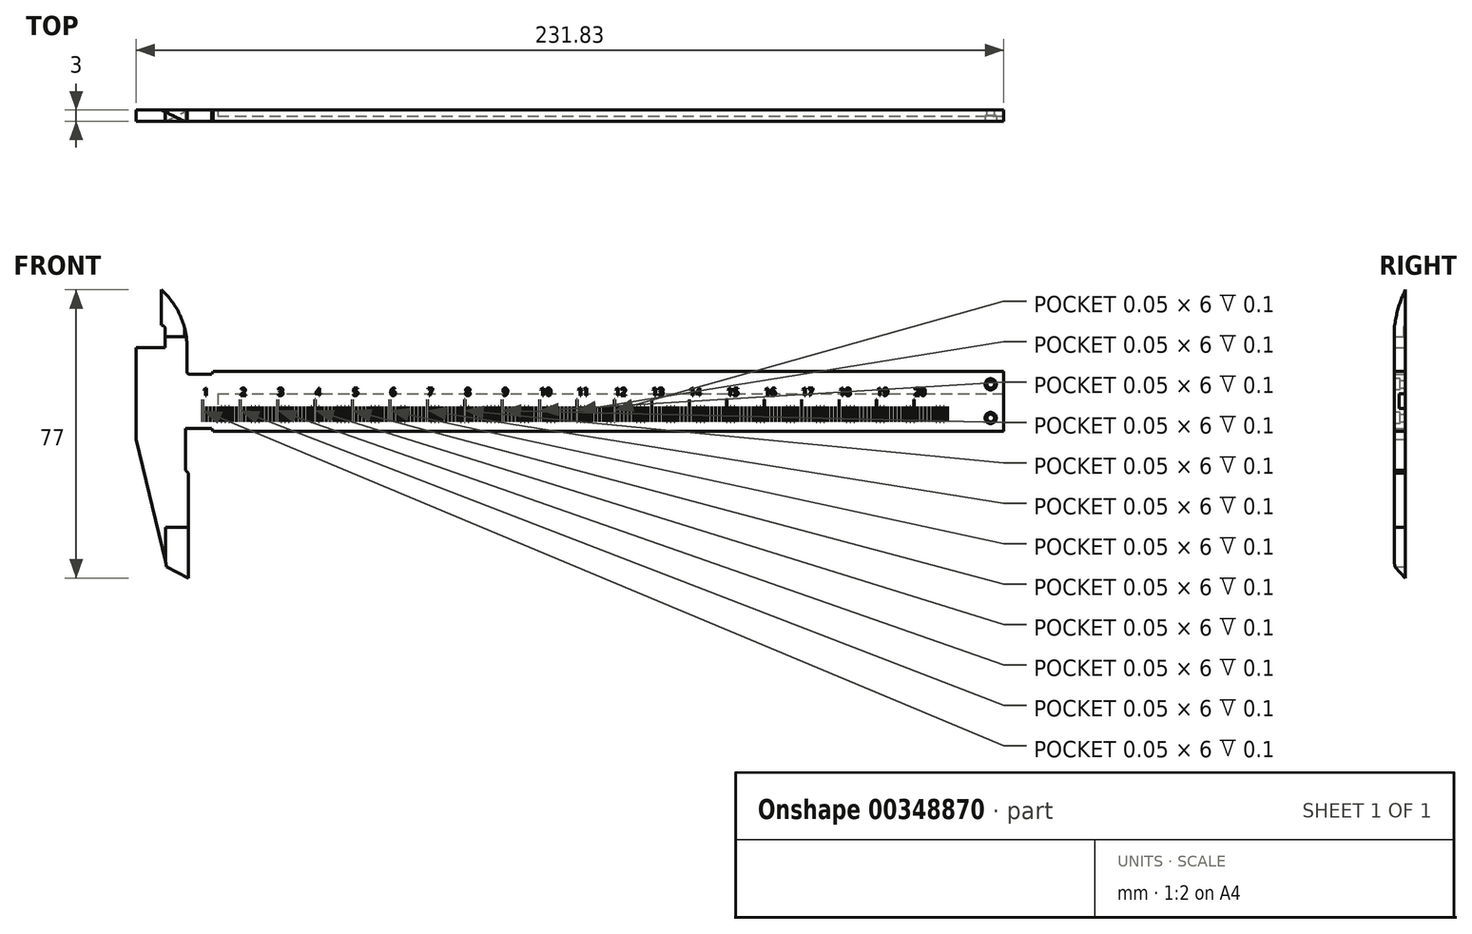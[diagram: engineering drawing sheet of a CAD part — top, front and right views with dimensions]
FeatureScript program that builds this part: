
annotation { "Feature Type Name" : "Feature", "Feature Type Description" : "" }
export const myFeature = defineFeature(function(context is Context, id is Id, definition is map)
    precondition{}
    {
        {
            var Q0;
            Q0=qCreatedBy(makeId("Front.planeOp"),FACE);
            var sketch = newSketch(context, id + "F0", { "sketchPlane" : qUnion([Q0])});
            skLineSegment(sketch, "E0", {"start": v(0, 0) * mm, "end": v(0, 0) * mm});
            skLineSegment(sketch, "E1", {"start": v(0, 8) * mm, "end": v(0, -8) * mm});
            skLineSegment(sketch, "E2", {"start": v(0, -8) * mm, "end": v(-211.2, -8) * mm});
            skLineSegment(sketch, "E3", {"start": v(-211.2, -8) * mm, "end": v(-211.63, -7.25) * mm});
            skLineSegment(sketch, "E4", {"start": v(-211.63, -7.25) * mm, "end": v(-218.63, -7.25) * mm});
            skLineSegment(sketch, "E5.MirrorCS", {"start": v(0, 8) * mm, "end": v(-211.2, 8) * mm});
            skLineSegment(sketch, "E6.MirrorCS", {"start": v(-211.63, 7.25) * mm, "end": v(-217.7, 7.25) * mm});
            skLineSegment(sketch, "E7.MirrorCS", {"start": v(-211.2, 8) * mm, "end": v(-211.63, 7.25) * mm});
            skLineSegment(sketch, "E8", {"start": v(-218.63, -7.25) * mm, "end": v(-218.63, -18.45) * mm});
            skLineSegment(sketch, "E9", {"start": v(-218.63, -18.45) * mm, "end": v(-217.83, -19.25) * mm});
            skLineSegment(sketch, "E10", {"start": v(-217.83, -19.25) * mm, "end": v(-217.83, -47.25) * mm});
            skLineSegment(sketch, "E11", {"start": v(-217.83, -47.25) * mm, "end": v(-223.63, -44.3) * mm});
            skLineSegment(sketch, "E12", {"start": v(-223.63, -44.3) * mm, "end": v(-231.83, -10.25) * mm});
            skLineSegment(sketch, "E13", {"start": v(0, 0) * mm, "end": v(-112.14, 0) * mm});
            skLineSegment(sketch, "E14", {"start": v(-231.83, -10.25) * mm, "end": v(-231.83, 14.25) * mm});
            skLineSegment(sketch, "E15", {"start": v(-231.83, 14.25) * mm, "end": v(-224.03, 14.25) * mm});
            skLineSegment(sketch, "E16", {"start": v(-224.03, 14.25) * mm, "end": v(-224.03, 19.25) * mm});
            skLineSegment(sketch, "E17", {"start": v(-225.03, 20.25) * mm, "end": v(-225.03, 20.25) * mm});
            skLineSegment(sketch, "E18", {"start": v(-225.03, 20.25) * mm, "end": v(-225.03, 29.75) * mm});
            skArc(sketch, "E19", {"start": v(-218.2, 14.25) * mm, "mid": v(-219.99, 22.72) * mm, "end": v(-225.03, 29.75) * mm});
            skLineSegment(sketch, "E20", {"start": v(-218.2, 7.75) * mm, "end": v(-218.2, 14.25) * mm});
            skPoint(sketch, "E21.visualSharp", {"position": v(-224.03, 20.25) * mm});
            skArc(sketch, "E21.filletArc", {"start": v(-224.03, 19.25) * mm, "mid": v(-224.33, 19.96) * mm, "end": v(-225.03, 20.25) * mm});
            skPoint(sketch, "E22.visualSharp", {"position": v(-218.2, 7.25) * mm});
            skArc(sketch, "E22.filletArc", {"start": v(-218.2, 7.75) * mm, "mid": v(-218.06, 7.4) * mm, "end": v(-217.7, 7.25) * mm});
            skSolve(sketch);
        }
        {
            var Q0;
            Q0=qSketchRegion(id+"F0",true);
            extrude(context, id + "F1", {"entities" : qUnion([Q0]), "depth" : 3 * mm});
        }
        {
            var Q0;
            Q0=makeQuery(id+"F1.opExtrude","CAP_FACE",FACE,{"disambiguationData":[OSD([sQuery(id+"F0.wireOp",EDGE,"E1"),sQuery(id+"F0.wireOp",EDGE,"E2"),sQuery(id+"F0.wireOp",EDGE,"E3"),sQuery(id+"F0.wireOp",EDGE,"E4"),sQuery(id+"F0.wireOp",EDGE,"E5.MirrorCS"),sQuery(id+"F0.wireOp",EDGE,"E6.MirrorCS"),sQuery(id+"F0.wireOp",EDGE,"E7.MirrorCS"),sQuery(id+"F0.wireOp",EDGE,"E8"),sQuery(id+"F0.wireOp",EDGE,"E9"),sQuery(id+"F0.wireOp",EDGE,"E10"),sQuery(id+"F0.wireOp",EDGE,"E11"),sQuery(id+"F0.wireOp",EDGE,"E12"),sQuery(id+"F0.wireOp",EDGE,"E14"),sQuery(id+"F0.wireOp",EDGE,"E15"),sQuery(id+"F0.wireOp",EDGE,"E16"),sQuery(id+"F0.wireOp",EDGE,"E17"),sQuery(id+"F0.wireOp",EDGE,"E18"),sQuery(id+"F0.wireOp",EDGE,"E19"),sQuery(id+"F0.wireOp",EDGE,"E20"),sQuery(id+"F0.wireOp",EDGE,"E21.filletArc"),sQuery(id+"F0.wireOp",EDGE,"E22.filletArc")])],"isStart":false});
            var sketch = newSketch(context, id + "F2", { "sketchPlane" : qUnion([Q0])});
            skCircle(sketch, "E23", {"center": v(-3.5, 4.5) * mm, "radius": 1.5 * mm});
            skCircle(sketch, "E24", {"center": v(-3.5, -4.5) * mm, "radius": 1.5 * mm});
            skSolve(sketch);
        }
        {
            var Q0;
            Q0=qSketchRegion(id+"F2",true);
            extrude(context, id + "F3", {"entities" : qUnion([Q0]), "operationType" : NewBodyOperationType.REMOVE, "oppositeDirection" : true, "depth" : 1.5 * mm});
        }
        {
            var Q0;
            Q0=qCreatedBy(makeId("Front.planeOp"),FACE);
            var sketch = newSketch(context, id + "F4", { "sketchPlane" : qUnion([Q0])});
            skCircle(sketch, "E25", {"center": v(-3.5, 4.5) * mm, "radius": 1 * mm});
            skCircle(sketch, "E26", {"center": v(-3.5, -4.5) * mm, "radius": 1 * mm});
            skSolve(sketch);
        }
        {
            var Q0;
            Q0=qSketchRegion(id+"F4",true);
            extrude(context, id + "F5", {"entities" : qUnion([Q0]), "operationType" : NewBodyOperationType.REMOVE, "endBound" : BoundingType.THROUGH_ALL, "depth" : 25 * mm});
        }
        {
            var Q0;
            Q0=makeQuery(id+"F1.opExtrude","SWEPT_FACE",FACE,{"disambiguationData":[OSD([sQuery(id+"F0.wireOp",EDGE,"E15")])]});
            var Q1;
            Q1=makeQuery(id+"F1.opExtrude","CAP_VERTEX",VERTEX,{"disambiguationData":[OSD([sQuery(id+"F0.wireOp",EDGE,"E18"),sQuery(id+"F0.wireOp",EDGE,"E19")])],"isStart":false});
            cPlane(context, id + "F6", {"entities" : qUnion([Q0, Q1]), "cplaneType" : CPlaneType.PLANE_POINT, "offset" : 25 * mm, "width" : 150 * mm, "height" : 150 * mm});
        }
        {
            var Q0;
            Q0=qCreatedBy(id+"F6.planeOp",FACE);
            var sketch = newSketch(context, id + "F7", { "sketchPlane" : qUnion([Q0])});
            skLineSegment(sketch, "E27.0", {"start": v(-225.03, -3) * mm, "end": v(-225.03, 0) * mm});
            skLineSegment(sketch, "E28.0", {"start": v(-218.88, -3) * mm, "end": v(-225.03, -3) * mm});
            skLineSegment(sketch, "E29", {"start": v(-225.03, 0) * mm, "end": v(-218.88, -3) * mm});
            skPoint(sketch, "E30.orphan", {"position": v(-218.2, -3) * mm});
            skSolve(sketch);
        }
        {
            var Q0;
            Q0=qSketchRegion(id+"F7",true);
            extrude(context, id + "F8", {"entities" : qUnion([Q0]), "operationType" : NewBodyOperationType.REMOVE, "oppositeDirection" : true, "depth" : 12.5 * mm});
        }
        {
            var Q0;
            Q0=makeQuery(id+"F1.opExtrude","SWEPT_FACE",FACE,{"disambiguationData":[OSD([sQuery(id+"F0.wireOp",EDGE,"E1")])]});
            var sketch = newSketch(context, id + "F9", { "sketchPlane" : qUnion([Q0])});
            skLineSegment(sketch, "E31", {"start": v(0, 0) * mm, "end": v(-6, 0) * mm, "construction": true});
            skLineSegment(sketch, "E32.bottom", {"start": v(0, -2) * mm, "end": v(-1.65, -2) * mm});
            skLineSegment(sketch, "E32.top", {"start": v(0, 2) * mm, "end": v(-1.65, 2) * mm});
            skLineSegment(sketch, "E32.left", {"start": v(0, -2) * mm, "end": v(0, 2) * mm});
            skLineSegment(sketch, "E32.right", {"start": v(-1.65, -2) * mm, "end": v(-1.65, 2) * mm});
            skSolve(sketch);
        }
        {
            var Q0;
            Q0=qSketchRegion(id+"F9",true);
            extrude(context, id + "F10", {"entities" : qUnion([Q0]), "operationType" : NewBodyOperationType.REMOVE, "oppositeDirection" : true, "depth" : 210 * mm});
        }
        {
            var Q0;
            Q0=makeQuery(id+"F1.opExtrude","SWEPT_FACE",FACE,{"disambiguationData":[OSD([sQuery(id+"F0.wireOp",EDGE,"E2")])]});
            var Q1;
            Q1=makeQuery(id+"F1.opExtrude","CAP_VERTEX",VERTEX,{"disambiguationData":[OSD([sQuery(id+"F0.wireOp",EDGE,"E10"),sQuery(id+"F0.wireOp",EDGE,"E11")])],"isStart":false});
            cPlane(context, id + "F11", {"entities" : qUnion([Q0, Q1]), "cplaneType" : CPlaneType.PLANE_POINT, "offset" : 25 * mm, "width" : 150 * mm, "height" : 150 * mm});
        }
        {
            var Q0;
            Q0=qCreatedBy(id+"F11.planeOp",FACE);
            var sketch = newSketch(context, id + "F12", { "sketchPlane" : qUnion([Q0])});
            skLineSegment(sketch, "E33.0", {"start": v(-217.83, 3) * mm, "end": v(-217.83, 0) * mm});
            skLineSegment(sketch, "E34", {"start": v(-217.83, 3) * mm, "end": v(-223.98, 3) * mm});
            skLineSegment(sketch, "E35", {"start": v(-223.98, 3) * mm, "end": v(-217.83, 0) * mm});
            skSolve(sketch);
        }
        {
            var Q0;
            Q0=qSketchRegion(id+"F12",true);
            extrude(context, id + "F13", {"entities" : qUnion([Q0]), "operationType" : NewBodyOperationType.REMOVE, "oppositeDirection" : true, "depth" : 13.5 * mm});
        }
        {
            var Q0;
            Q0=makeQuery(id+"F1.opExtrude","CAP_FACE",FACE,{"disambiguationData":[OSD([sQuery(id+"F0.wireOp",EDGE,"E1"),sQuery(id+"F0.wireOp",EDGE,"E2"),sQuery(id+"F0.wireOp",EDGE,"E3"),sQuery(id+"F0.wireOp",EDGE,"E4"),sQuery(id+"F0.wireOp",EDGE,"E5.MirrorCS"),sQuery(id+"F0.wireOp",EDGE,"E6.MirrorCS"),sQuery(id+"F0.wireOp",EDGE,"E7.MirrorCS"),sQuery(id+"F0.wireOp",EDGE,"E8"),sQuery(id+"F0.wireOp",EDGE,"E9"),sQuery(id+"F0.wireOp",EDGE,"E10"),sQuery(id+"F0.wireOp",EDGE,"E11"),sQuery(id+"F0.wireOp",EDGE,"E12"),sQuery(id+"F0.wireOp",EDGE,"E14"),sQuery(id+"F0.wireOp",EDGE,"E15"),sQuery(id+"F0.wireOp",EDGE,"E16"),sQuery(id+"F0.wireOp",EDGE,"E17"),sQuery(id+"F0.wireOp",EDGE,"E18"),sQuery(id+"F0.wireOp",EDGE,"E19"),sQuery(id+"F0.wireOp",EDGE,"E20"),sQuery(id+"F0.wireOp",EDGE,"E21.filletArc"),sQuery(id+"F0.wireOp",EDGE,"E22.filletArc")])],"isStart":false});
            var sketch = newSketch(context, id + "F14", { "sketchPlane" : qUnion([Q0])});
            skLineSegment(sketch, "E36.bottom", {"start": v(-214.03, 0.5) * mm, "end": v(-213.98, 0.5) * mm});
            skLineSegment(sketch, "E36.top", {"start": v(-214.03, -5.5) * mm, "end": v(-213.98, -5.5) * mm});
            skLineSegment(sketch, "E36.left", {"start": v(-213.98, 0.5) * mm, "end": v(-213.98, -5.5) * mm});
            skLineSegment(sketch, "E36.right", {"start": v(-214.03, 0.5) * mm, "end": v(-214.03, -5.5) * mm});
            skLineSegment(sketch, "E37.1.0.0", {"start": v(-203.98, 0.5) * mm, "end": v(-203.98, -5.5) * mm});
            skLineSegment(sketch, "E37.1.0.1", {"start": v(-204.03, 0.5) * mm, "end": v(-204.03, -5.5) * mm});
            skLineSegment(sketch, "E37.1.0.2", {"start": v(-204.03, -5.5) * mm, "end": v(-203.98, -5.5) * mm});
            skLineSegment(sketch, "E37.1.0.3", {"start": v(-204.03, 0.5) * mm, "end": v(-203.98, 0.5) * mm});
            skLineSegment(sketch, "E37.2.0.0", {"start": v(-193.98, 0.5) * mm, "end": v(-193.98, -5.5) * mm});
            skLineSegment(sketch, "E37.2.0.1", {"start": v(-194.03, 0.5) * mm, "end": v(-194.03, -5.5) * mm});
            skLineSegment(sketch, "E37.2.0.2", {"start": v(-194.03, -5.5) * mm, "end": v(-193.98, -5.5) * mm});
            skLineSegment(sketch, "E37.2.0.3", {"start": v(-194.03, 0.5) * mm, "end": v(-193.98, 0.5) * mm});
            skLineSegment(sketch, "E37.3.0.0", {"start": v(-183.98, 0.5) * mm, "end": v(-183.98, -5.5) * mm});
            skLineSegment(sketch, "E37.3.0.1", {"start": v(-184.03, 0.5) * mm, "end": v(-184.03, -5.5) * mm});
            skLineSegment(sketch, "E37.3.0.2", {"start": v(-184.03, -5.5) * mm, "end": v(-183.98, -5.5) * mm});
            skLineSegment(sketch, "E37.3.0.3", {"start": v(-184.03, 0.5) * mm, "end": v(-183.98, 0.5) * mm});
            skLineSegment(sketch, "E37.4.0.0", {"start": v(-173.98, 0.5) * mm, "end": v(-173.98, -5.5) * mm});
            skLineSegment(sketch, "E37.4.0.1", {"start": v(-174.03, 0.5) * mm, "end": v(-174.03, -5.5) * mm});
            skLineSegment(sketch, "E37.4.0.2", {"start": v(-174.03, -5.5) * mm, "end": v(-173.98, -5.5) * mm});
            skLineSegment(sketch, "E37.4.0.3", {"start": v(-174.03, 0.5) * mm, "end": v(-173.98, 0.5) * mm});
            skLineSegment(sketch, "E37.5.0.0", {"start": v(-163.98, 0.5) * mm, "end": v(-163.98, -5.5) * mm});
            skLineSegment(sketch, "E37.5.0.1", {"start": v(-164.03, 0.5) * mm, "end": v(-164.03, -5.5) * mm});
            skLineSegment(sketch, "E37.5.0.2", {"start": v(-164.03, -5.5) * mm, "end": v(-163.98, -5.5) * mm});
            skLineSegment(sketch, "E37.5.0.3", {"start": v(-164.03, 0.5) * mm, "end": v(-163.98, 0.5) * mm});
            skLineSegment(sketch, "E37.6.0.0", {"start": v(-153.98, 0.5) * mm, "end": v(-153.98, -5.5) * mm});
            skLineSegment(sketch, "E37.6.0.1", {"start": v(-154.03, 0.5) * mm, "end": v(-154.03, -5.5) * mm});
            skLineSegment(sketch, "E37.6.0.2", {"start": v(-154.03, -5.5) * mm, "end": v(-153.98, -5.5) * mm});
            skLineSegment(sketch, "E37.6.0.3", {"start": v(-154.03, 0.5) * mm, "end": v(-153.98, 0.5) * mm});
            skLineSegment(sketch, "E37.7.0.0", {"start": v(-143.98, 0.5) * mm, "end": v(-143.98, -5.5) * mm});
            skLineSegment(sketch, "E37.7.0.1", {"start": v(-144.03, 0.5) * mm, "end": v(-144.03, -5.5) * mm});
            skLineSegment(sketch, "E37.7.0.2", {"start": v(-144.03, -5.5) * mm, "end": v(-143.98, -5.5) * mm});
            skLineSegment(sketch, "E37.7.0.3", {"start": v(-144.03, 0.5) * mm, "end": v(-143.98, 0.5) * mm});
            skLineSegment(sketch, "E37.8.0.0", {"start": v(-133.98, 0.5) * mm, "end": v(-133.98, -5.5) * mm});
            skLineSegment(sketch, "E37.8.0.1", {"start": v(-134.03, 0.5) * mm, "end": v(-134.03, -5.5) * mm});
            skLineSegment(sketch, "E37.8.0.2", {"start": v(-134.03, -5.5) * mm, "end": v(-133.98, -5.5) * mm});
            skLineSegment(sketch, "E37.8.0.3", {"start": v(-134.03, 0.5) * mm, "end": v(-133.98, 0.5) * mm});
            skLineSegment(sketch, "E37.9.0.0", {"start": v(-123.98, 0.5) * mm, "end": v(-123.98, -5.5) * mm});
            skLineSegment(sketch, "E37.9.0.1", {"start": v(-124.03, 0.5) * mm, "end": v(-124.03, -5.5) * mm});
            skLineSegment(sketch, "E37.9.0.2", {"start": v(-124.03, -5.5) * mm, "end": v(-123.98, -5.5) * mm});
            skLineSegment(sketch, "E37.9.0.3", {"start": v(-124.03, 0.5) * mm, "end": v(-123.98, 0.5) * mm});
            skLineSegment(sketch, "E37.10.0.0", {"start": v(-113.98, 0.5) * mm, "end": v(-113.98, -5.5) * mm});
            skLineSegment(sketch, "E37.10.0.1", {"start": v(-114.03, 0.5) * mm, "end": v(-114.03, -5.5) * mm});
            skLineSegment(sketch, "E37.10.0.2", {"start": v(-114.03, -5.5) * mm, "end": v(-113.98, -5.5) * mm});
            skLineSegment(sketch, "E37.10.0.3", {"start": v(-114.03, 0.5) * mm, "end": v(-113.98, 0.5) * mm});
            skLineSegment(sketch, "E37.11.0.0", {"start": v(-103.98, 0.5) * mm, "end": v(-103.98, -5.5) * mm});
            skLineSegment(sketch, "E37.11.0.1", {"start": v(-104.03, 0.5) * mm, "end": v(-104.03, -5.5) * mm});
            skLineSegment(sketch, "E37.11.0.2", {"start": v(-104.03, -5.5) * mm, "end": v(-103.98, -5.5) * mm});
            skLineSegment(sketch, "E37.11.0.3", {"start": v(-104.03, 0.5) * mm, "end": v(-103.98, 0.5) * mm});
            skLineSegment(sketch, "E37.12.0.0", {"start": v(-93.98, 0.5) * mm, "end": v(-93.98, -5.5) * mm});
            skLineSegment(sketch, "E37.12.0.1", {"start": v(-94.03, 0.5) * mm, "end": v(-94.03, -5.5) * mm});
            skLineSegment(sketch, "E37.12.0.2", {"start": v(-94.03, -5.5) * mm, "end": v(-93.98, -5.5) * mm});
            skLineSegment(sketch, "E37.12.0.3", {"start": v(-94.03, 0.5) * mm, "end": v(-93.98, 0.5) * mm});
            skLineSegment(sketch, "E37.13.0.0", {"start": v(-83.98, 0.5) * mm, "end": v(-83.98, -5.5) * mm});
            skLineSegment(sketch, "E37.13.0.1", {"start": v(-84.03, 0.5) * mm, "end": v(-84.03, -5.5) * mm});
            skLineSegment(sketch, "E37.13.0.2", {"start": v(-84.03, -5.5) * mm, "end": v(-83.98, -5.5) * mm});
            skLineSegment(sketch, "E37.13.0.3", {"start": v(-84.03, 0.5) * mm, "end": v(-83.98, 0.5) * mm});
            skLineSegment(sketch, "E37.14.0.0", {"start": v(-73.98, 0.5) * mm, "end": v(-73.98, -5.5) * mm});
            skLineSegment(sketch, "E37.14.0.1", {"start": v(-74.03, 0.5) * mm, "end": v(-74.03, -5.5) * mm});
            skLineSegment(sketch, "E37.14.0.2", {"start": v(-74.03, -5.5) * mm, "end": v(-73.98, -5.5) * mm});
            skLineSegment(sketch, "E37.14.0.3", {"start": v(-74.03, 0.5) * mm, "end": v(-73.98, 0.5) * mm});
            skLineSegment(sketch, "E37.15.0.0", {"start": v(-63.98, 0.5) * mm, "end": v(-63.98, -5.5) * mm});
            skLineSegment(sketch, "E37.15.0.1", {"start": v(-64.03, 0.5) * mm, "end": v(-64.03, -5.5) * mm});
            skLineSegment(sketch, "E37.15.0.2", {"start": v(-64.03, -5.5) * mm, "end": v(-63.98, -5.5) * mm});
            skLineSegment(sketch, "E37.15.0.3", {"start": v(-64.03, 0.5) * mm, "end": v(-63.98, 0.5) * mm});
            skLineSegment(sketch, "E37.16.0.0", {"start": v(-53.98, 0.5) * mm, "end": v(-53.98, -5.5) * mm});
            skLineSegment(sketch, "E37.16.0.1", {"start": v(-54.03, 0.5) * mm, "end": v(-54.03, -5.5) * mm});
            skLineSegment(sketch, "E37.16.0.2", {"start": v(-54.03, -5.5) * mm, "end": v(-53.98, -5.5) * mm});
            skLineSegment(sketch, "E37.16.0.3", {"start": v(-54.03, 0.5) * mm, "end": v(-53.98, 0.5) * mm});
            skLineSegment(sketch, "E37.17.0.0", {"start": v(-43.98, 0.5) * mm, "end": v(-43.98, -5.5) * mm});
            skLineSegment(sketch, "E37.17.0.1", {"start": v(-44.03, 0.5) * mm, "end": v(-44.03, -5.5) * mm});
            skLineSegment(sketch, "E37.17.0.2", {"start": v(-44.03, -5.5) * mm, "end": v(-43.98, -5.5) * mm});
            skLineSegment(sketch, "E37.17.0.3", {"start": v(-44.03, 0.5) * mm, "end": v(-43.98, 0.5) * mm});
            skLineSegment(sketch, "E37.18.0.0", {"start": v(-33.98, 0.5) * mm, "end": v(-33.98, -5.5) * mm});
            skLineSegment(sketch, "E37.18.0.1", {"start": v(-34.03, 0.5) * mm, "end": v(-34.03, -5.5) * mm});
            skLineSegment(sketch, "E37.18.0.2", {"start": v(-34.03, -5.5) * mm, "end": v(-33.98, -5.5) * mm});
            skLineSegment(sketch, "E37.18.0.3", {"start": v(-34.03, 0.5) * mm, "end": v(-33.98, 0.5) * mm});
            skLineSegment(sketch, "E37.19.0.0", {"start": v(-23.98, 0.5) * mm, "end": v(-23.98, -5.5) * mm});
            skLineSegment(sketch, "E37.19.0.1", {"start": v(-24.03, 0.5) * mm, "end": v(-24.03, -5.5) * mm});
            skLineSegment(sketch, "E37.19.0.2", {"start": v(-24.03, -5.5) * mm, "end": v(-23.98, -5.5) * mm});
            skLineSegment(sketch, "E37.19.0.3", {"start": v(-24.03, 0.5) * mm, "end": v(-23.98, 0.5) * mm});
            skLineSegment(sketch, "E37.direction1", {"start": v(-214.03, -5.5) * mm, "end": v(-204.03, -5.5) * mm, "construction": true});
            skLineSegment(sketch, "E38.bottom", {"start": v(-213.03, -1.5) * mm, "end": v(-212.98, -1.5) * mm});
            skLineSegment(sketch, "E38.top", {"start": v(-213.03, -5.5) * mm, "end": v(-212.98, -5.5) * mm});
            skLineSegment(sketch, "E38.left", {"start": v(-213.03, -1.5) * mm, "end": v(-213.03, -5.5) * mm});
            skLineSegment(sketch, "E38.right", {"start": v(-212.98, -1.5) * mm, "end": v(-212.98, -5.5) * mm});
            skLineSegment(sketch, "E39.1.0.0", {"start": v(-211.98, -1.5) * mm, "end": v(-211.98, -5.5) * mm});
            skLineSegment(sketch, "E39.1.0.1", {"start": v(-212.03, -1.5) * mm, "end": v(-212.03, -5.5) * mm});
            skLineSegment(sketch, "E39.1.0.2", {"start": v(-212.03, -1.5) * mm, "end": v(-211.98, -1.5) * mm});
            skLineSegment(sketch, "E39.1.0.3", {"start": v(-212.03, -5.5) * mm, "end": v(-211.98, -5.5) * mm});
            skLineSegment(sketch, "E39.2.0.0", {"start": v(-210.98, -1.5) * mm, "end": v(-210.98, -5.5) * mm});
            skLineSegment(sketch, "E39.2.0.1", {"start": v(-211.03, -1.5) * mm, "end": v(-211.03, -5.5) * mm});
            skLineSegment(sketch, "E39.2.0.2", {"start": v(-211.03, -1.5) * mm, "end": v(-210.98, -1.5) * mm});
            skLineSegment(sketch, "E39.2.0.3", {"start": v(-211.03, -5.5) * mm, "end": v(-210.98, -5.5) * mm});
            skLineSegment(sketch, "E39.3.0.0", {"start": v(-209.98, -1.5) * mm, "end": v(-209.98, -5.5) * mm});
            skLineSegment(sketch, "E39.3.0.1", {"start": v(-210.03, -1.5) * mm, "end": v(-210.03, -5.5) * mm});
            skLineSegment(sketch, "E39.3.0.2", {"start": v(-210.03, -1.5) * mm, "end": v(-209.98, -1.5) * mm});
            skLineSegment(sketch, "E39.3.0.3", {"start": v(-210.03, -5.5) * mm, "end": v(-209.98, -5.5) * mm});
            skLineSegment(sketch, "E39.4.0.0", {"start": v(-208.98, -1.5) * mm, "end": v(-208.98, -5.5) * mm});
            skLineSegment(sketch, "E39.4.0.1", {"start": v(-209.03, -1.5) * mm, "end": v(-209.03, -5.5) * mm});
            skLineSegment(sketch, "E39.4.0.2", {"start": v(-209.03, -1.5) * mm, "end": v(-208.98, -1.5) * mm});
            skLineSegment(sketch, "E39.4.0.3", {"start": v(-209.03, -5.5) * mm, "end": v(-208.98, -5.5) * mm});
            skLineSegment(sketch, "E39.5.0.0", {"start": v(-207.98, -1.5) * mm, "end": v(-207.98, -5.5) * mm});
            skLineSegment(sketch, "E39.5.0.1", {"start": v(-208.03, -1.5) * mm, "end": v(-208.03, -5.5) * mm});
            skLineSegment(sketch, "E39.5.0.2", {"start": v(-208.03, -1.5) * mm, "end": v(-207.98, -1.5) * mm});
            skLineSegment(sketch, "E39.5.0.3", {"start": v(-208.03, -5.5) * mm, "end": v(-207.98, -5.5) * mm});
            skLineSegment(sketch, "E39.6.0.0", {"start": v(-206.98, -1.5) * mm, "end": v(-206.98, -5.5) * mm});
            skLineSegment(sketch, "E39.6.0.1", {"start": v(-207.03, -1.5) * mm, "end": v(-207.03, -5.5) * mm});
            skLineSegment(sketch, "E39.6.0.2", {"start": v(-207.03, -1.5) * mm, "end": v(-206.98, -1.5) * mm});
            skLineSegment(sketch, "E39.6.0.3", {"start": v(-207.03, -5.5) * mm, "end": v(-206.98, -5.5) * mm});
            skLineSegment(sketch, "E39.7.0.0", {"start": v(-205.98, -1.5) * mm, "end": v(-205.98, -5.5) * mm});
            skLineSegment(sketch, "E39.7.0.1", {"start": v(-206.03, -1.5) * mm, "end": v(-206.03, -5.5) * mm});
            skLineSegment(sketch, "E39.7.0.2", {"start": v(-206.03, -1.5) * mm, "end": v(-205.98, -1.5) * mm});
            skLineSegment(sketch, "E39.7.0.3", {"start": v(-206.03, -5.5) * mm, "end": v(-205.98, -5.5) * mm});
            skLineSegment(sketch, "E39.8.0.0", {"start": v(-204.98, -1.5) * mm, "end": v(-204.98, -5.5) * mm});
            skLineSegment(sketch, "E39.8.0.1", {"start": v(-205.03, -1.5) * mm, "end": v(-205.03, -5.5) * mm});
            skLineSegment(sketch, "E39.8.0.2", {"start": v(-205.03, -1.5) * mm, "end": v(-204.98, -1.5) * mm});
            skLineSegment(sketch, "E39.8.0.3", {"start": v(-205.03, -5.5) * mm, "end": v(-204.98, -5.5) * mm});
            skLineSegment(sketch, "E39.direction1", {"start": v(-213.03, -5.5) * mm, "end": v(-212.03, -5.5) * mm, "construction": true});
            skLineSegment(sketch, "E40.1.0.0", {"start": v(-202.03, -1.5) * mm, "end": v(-202.03, -5.5) * mm});
            skLineSegment(sketch, "E40.1.0.1", {"start": v(-198.03, -1.5) * mm, "end": v(-198.03, -5.5) * mm});
            skLineSegment(sketch, "E40.1.0.2", {"start": v(-203.03, -5.5) * mm, "end": v(-202.03, -5.5) * mm, "construction": true});
            skLineSegment(sketch, "E40.1.0.3", {"start": v(-201.98, -1.5) * mm, "end": v(-201.98, -5.5) * mm});
            skLineSegment(sketch, "E40.1.0.4", {"start": v(-197.98, -1.5) * mm, "end": v(-197.98, -5.5) * mm});
            skLineSegment(sketch, "E40.1.0.5", {"start": v(-202.98, -1.5) * mm, "end": v(-202.98, -5.5) * mm});
            skLineSegment(sketch, "E40.1.0.6", {"start": v(-197.03, -1.5) * mm, "end": v(-197.03, -5.5) * mm});
            skLineSegment(sketch, "E40.1.0.7", {"start": v(-201.03, -1.5) * mm, "end": v(-201.03, -5.5) * mm});
            skLineSegment(sketch, "E40.1.0.8", {"start": v(-199.98, -1.5) * mm, "end": v(-199.98, -5.5) * mm});
            skLineSegment(sketch, "E40.1.0.9", {"start": v(-195.98, -1.5) * mm, "end": v(-195.98, -5.5) * mm});
            skLineSegment(sketch, "E40.1.0.10", {"start": v(-200.03, -1.5) * mm, "end": v(-200.03, -5.5) * mm});
            skLineSegment(sketch, "E40.1.0.11", {"start": v(-196.03, -1.5) * mm, "end": v(-196.03, -5.5) * mm});
            skLineSegment(sketch, "E40.1.0.12", {"start": v(-195.03, -1.5) * mm, "end": v(-195.03, -5.5) * mm});
            skLineSegment(sketch, "E40.1.0.13", {"start": v(-199.03, -1.5) * mm, "end": v(-199.03, -5.5) * mm});
            skLineSegment(sketch, "E40.1.0.14", {"start": v(-196.98, -1.5) * mm, "end": v(-196.98, -5.5) * mm});
            skLineSegment(sketch, "E40.1.0.15", {"start": v(-200.98, -1.5) * mm, "end": v(-200.98, -5.5) * mm});
            skLineSegment(sketch, "E40.1.0.16", {"start": v(-198.98, -1.5) * mm, "end": v(-198.98, -5.5) * mm});
            skLineSegment(sketch, "E40.1.0.17", {"start": v(-194.98, -1.5) * mm, "end": v(-194.98, -5.5) * mm});
            skLineSegment(sketch, "E40.1.0.18", {"start": v(-203.03, -1.5) * mm, "end": v(-203.03, -5.5) * mm});
            skLineSegment(sketch, "E40.1.0.19", {"start": v(-198.03, -5.5) * mm, "end": v(-197.98, -5.5) * mm});
            skLineSegment(sketch, "E40.1.0.20", {"start": v(-202.03, -1.5) * mm, "end": v(-201.98, -1.5) * mm});
            skLineSegment(sketch, "E40.1.0.21", {"start": v(-198.03, -1.5) * mm, "end": v(-197.98, -1.5) * mm});
            skLineSegment(sketch, "E40.1.0.22", {"start": v(-200.03, -1.5) * mm, "end": v(-199.98, -1.5) * mm});
            skLineSegment(sketch, "E40.1.0.23", {"start": v(-196.03, -1.5) * mm, "end": v(-195.98, -1.5) * mm});
            skLineSegment(sketch, "E40.1.0.24", {"start": v(-200.03, -5.5) * mm, "end": v(-199.98, -5.5) * mm});
            skLineSegment(sketch, "E40.1.0.25", {"start": v(-196.03, -5.5) * mm, "end": v(-195.98, -5.5) * mm});
            skLineSegment(sketch, "E40.1.0.26", {"start": v(-202.03, -5.5) * mm, "end": v(-201.98, -5.5) * mm});
            skLineSegment(sketch, "E40.1.0.27", {"start": v(-195.03, -5.5) * mm, "end": v(-194.98, -5.5) * mm});
            skLineSegment(sketch, "E40.1.0.28", {"start": v(-199.03, -5.5) * mm, "end": v(-198.98, -5.5) * mm});
            skLineSegment(sketch, "E40.1.0.29", {"start": v(-197.03, -1.5) * mm, "end": v(-196.98, -1.5) * mm});
            skLineSegment(sketch, "E40.1.0.30", {"start": v(-201.03, -1.5) * mm, "end": v(-200.98, -1.5) * mm});
            skLineSegment(sketch, "E40.1.0.31", {"start": v(-197.03, -5.5) * mm, "end": v(-196.98, -5.5) * mm});
            skLineSegment(sketch, "E40.1.0.32", {"start": v(-201.03, -5.5) * mm, "end": v(-200.98, -5.5) * mm});
            skLineSegment(sketch, "E40.1.0.33", {"start": v(-203.03, -1.5) * mm, "end": v(-202.98, -1.5) * mm});
            skLineSegment(sketch, "E40.1.0.34", {"start": v(-199.03, -1.5) * mm, "end": v(-198.98, -1.5) * mm});
            skLineSegment(sketch, "E40.1.0.35", {"start": v(-195.03, -1.5) * mm, "end": v(-194.98, -1.5) * mm});
            skLineSegment(sketch, "E40.1.0.36", {"start": v(-203.03, -5.5) * mm, "end": v(-202.98, -5.5) * mm});
            skLineSegment(sketch, "E40.2.0.0", {"start": v(-192.03, -1.5) * mm, "end": v(-192.03, -5.5) * mm});
            skLineSegment(sketch, "E40.2.0.1", {"start": v(-188.03, -1.5) * mm, "end": v(-188.03, -5.5) * mm});
            skLineSegment(sketch, "E40.2.0.2", {"start": v(-193.03, -5.5) * mm, "end": v(-192.03, -5.5) * mm, "construction": true});
            skLineSegment(sketch, "E40.2.0.3", {"start": v(-191.98, -1.5) * mm, "end": v(-191.98, -5.5) * mm});
            skLineSegment(sketch, "E40.2.0.4", {"start": v(-187.98, -1.5) * mm, "end": v(-187.98, -5.5) * mm});
            skLineSegment(sketch, "E40.2.0.5", {"start": v(-192.98, -1.5) * mm, "end": v(-192.98, -5.5) * mm});
            skLineSegment(sketch, "E40.2.0.6", {"start": v(-187.03, -1.5) * mm, "end": v(-187.03, -5.5) * mm});
            skLineSegment(sketch, "E40.2.0.7", {"start": v(-191.03, -1.5) * mm, "end": v(-191.03, -5.5) * mm});
            skLineSegment(sketch, "E40.2.0.8", {"start": v(-189.98, -1.5) * mm, "end": v(-189.98, -5.5) * mm});
            skLineSegment(sketch, "E40.2.0.9", {"start": v(-185.98, -1.5) * mm, "end": v(-185.98, -5.5) * mm});
            skLineSegment(sketch, "E40.2.0.10", {"start": v(-190.03, -1.5) * mm, "end": v(-190.03, -5.5) * mm});
            skLineSegment(sketch, "E40.2.0.11", {"start": v(-186.03, -1.5) * mm, "end": v(-186.03, -5.5) * mm});
            skLineSegment(sketch, "E40.2.0.12", {"start": v(-185.03, -1.5) * mm, "end": v(-185.03, -5.5) * mm});
            skLineSegment(sketch, "E40.2.0.13", {"start": v(-189.03, -1.5) * mm, "end": v(-189.03, -5.5) * mm});
            skLineSegment(sketch, "E40.2.0.14", {"start": v(-186.98, -1.5) * mm, "end": v(-186.98, -5.5) * mm});
            skLineSegment(sketch, "E40.2.0.15", {"start": v(-190.98, -1.5) * mm, "end": v(-190.98, -5.5) * mm});
            skLineSegment(sketch, "E40.2.0.16", {"start": v(-188.98, -1.5) * mm, "end": v(-188.98, -5.5) * mm});
            skLineSegment(sketch, "E40.2.0.17", {"start": v(-184.98, -1.5) * mm, "end": v(-184.98, -5.5) * mm});
            skLineSegment(sketch, "E40.2.0.18", {"start": v(-193.03, -1.5) * mm, "end": v(-193.03, -5.5) * mm});
            skLineSegment(sketch, "E40.2.0.19", {"start": v(-188.03, -5.5) * mm, "end": v(-187.98, -5.5) * mm});
            skLineSegment(sketch, "E40.2.0.20", {"start": v(-192.03, -1.5) * mm, "end": v(-191.98, -1.5) * mm});
            skLineSegment(sketch, "E40.2.0.21", {"start": v(-188.03, -1.5) * mm, "end": v(-187.98, -1.5) * mm});
            skLineSegment(sketch, "E40.2.0.22", {"start": v(-190.03, -1.5) * mm, "end": v(-189.98, -1.5) * mm});
            skLineSegment(sketch, "E40.2.0.23", {"start": v(-186.03, -1.5) * mm, "end": v(-185.98, -1.5) * mm});
            skLineSegment(sketch, "E40.2.0.24", {"start": v(-190.03, -5.5) * mm, "end": v(-189.98, -5.5) * mm});
            skLineSegment(sketch, "E40.2.0.25", {"start": v(-186.03, -5.5) * mm, "end": v(-185.98, -5.5) * mm});
            skLineSegment(sketch, "E40.2.0.26", {"start": v(-192.03, -5.5) * mm, "end": v(-191.98, -5.5) * mm});
            skLineSegment(sketch, "E40.2.0.27", {"start": v(-185.03, -5.5) * mm, "end": v(-184.98, -5.5) * mm});
            skLineSegment(sketch, "E40.2.0.28", {"start": v(-189.03, -5.5) * mm, "end": v(-188.98, -5.5) * mm});
            skLineSegment(sketch, "E40.2.0.29", {"start": v(-187.03, -1.5) * mm, "end": v(-186.98, -1.5) * mm});
            skLineSegment(sketch, "E40.2.0.30", {"start": v(-191.03, -1.5) * mm, "end": v(-190.98, -1.5) * mm});
            skLineSegment(sketch, "E40.2.0.31", {"start": v(-187.03, -5.5) * mm, "end": v(-186.98, -5.5) * mm});
            skLineSegment(sketch, "E40.2.0.32", {"start": v(-191.03, -5.5) * mm, "end": v(-190.98, -5.5) * mm});
            skLineSegment(sketch, "E40.2.0.33", {"start": v(-193.03, -1.5) * mm, "end": v(-192.98, -1.5) * mm});
            skLineSegment(sketch, "E40.2.0.34", {"start": v(-189.03, -1.5) * mm, "end": v(-188.98, -1.5) * mm});
            skLineSegment(sketch, "E40.2.0.35", {"start": v(-185.03, -1.5) * mm, "end": v(-184.98, -1.5) * mm});
            skLineSegment(sketch, "E40.2.0.36", {"start": v(-193.03, -5.5) * mm, "end": v(-192.98, -5.5) * mm});
            skLineSegment(sketch, "E40.3.0.0", {"start": v(-182.03, -1.5) * mm, "end": v(-182.03, -5.5) * mm});
            skLineSegment(sketch, "E40.3.0.1", {"start": v(-178.03, -1.5) * mm, "end": v(-178.03, -5.5) * mm});
            skLineSegment(sketch, "E40.3.0.2", {"start": v(-183.03, -5.5) * mm, "end": v(-182.03, -5.5) * mm, "construction": true});
            skLineSegment(sketch, "E40.3.0.3", {"start": v(-181.98, -1.5) * mm, "end": v(-181.98, -5.5) * mm});
            skLineSegment(sketch, "E40.3.0.4", {"start": v(-177.98, -1.5) * mm, "end": v(-177.98, -5.5) * mm});
            skLineSegment(sketch, "E40.3.0.5", {"start": v(-182.98, -1.5) * mm, "end": v(-182.98, -5.5) * mm});
            skLineSegment(sketch, "E40.3.0.6", {"start": v(-177.03, -1.5) * mm, "end": v(-177.03, -5.5) * mm});
            skLineSegment(sketch, "E40.3.0.7", {"start": v(-181.03, -1.5) * mm, "end": v(-181.03, -5.5) * mm});
            skLineSegment(sketch, "E40.3.0.8", {"start": v(-179.98, -1.5) * mm, "end": v(-179.98, -5.5) * mm});
            skLineSegment(sketch, "E40.3.0.9", {"start": v(-175.98, -1.5) * mm, "end": v(-175.98, -5.5) * mm});
            skLineSegment(sketch, "E40.3.0.10", {"start": v(-180.03, -1.5) * mm, "end": v(-180.03, -5.5) * mm});
            skLineSegment(sketch, "E40.3.0.11", {"start": v(-176.03, -1.5) * mm, "end": v(-176.03, -5.5) * mm});
            skLineSegment(sketch, "E40.3.0.12", {"start": v(-175.03, -1.5) * mm, "end": v(-175.03, -5.5) * mm});
            skLineSegment(sketch, "E40.3.0.13", {"start": v(-179.03, -1.5) * mm, "end": v(-179.03, -5.5) * mm});
            skLineSegment(sketch, "E40.3.0.14", {"start": v(-176.98, -1.5) * mm, "end": v(-176.98, -5.5) * mm});
            skLineSegment(sketch, "E40.3.0.15", {"start": v(-180.98, -1.5) * mm, "end": v(-180.98, -5.5) * mm});
            skLineSegment(sketch, "E40.3.0.16", {"start": v(-178.98, -1.5) * mm, "end": v(-178.98, -5.5) * mm});
            skLineSegment(sketch, "E40.3.0.17", {"start": v(-174.98, -1.5) * mm, "end": v(-174.98, -5.5) * mm});
            skLineSegment(sketch, "E40.3.0.18", {"start": v(-183.03, -1.5) * mm, "end": v(-183.03, -5.5) * mm});
            skLineSegment(sketch, "E40.3.0.19", {"start": v(-178.03, -5.5) * mm, "end": v(-177.98, -5.5) * mm});
            skLineSegment(sketch, "E40.3.0.20", {"start": v(-182.03, -1.5) * mm, "end": v(-181.98, -1.5) * mm});
            skLineSegment(sketch, "E40.3.0.21", {"start": v(-178.03, -1.5) * mm, "end": v(-177.98, -1.5) * mm});
            skLineSegment(sketch, "E40.3.0.22", {"start": v(-180.03, -1.5) * mm, "end": v(-179.98, -1.5) * mm});
            skLineSegment(sketch, "E40.3.0.23", {"start": v(-176.03, -1.5) * mm, "end": v(-175.98, -1.5) * mm});
            skLineSegment(sketch, "E40.3.0.24", {"start": v(-180.03, -5.5) * mm, "end": v(-179.98, -5.5) * mm});
            skLineSegment(sketch, "E40.3.0.25", {"start": v(-176.03, -5.5) * mm, "end": v(-175.98, -5.5) * mm});
            skLineSegment(sketch, "E40.3.0.26", {"start": v(-182.03, -5.5) * mm, "end": v(-181.98, -5.5) * mm});
            skLineSegment(sketch, "E40.3.0.27", {"start": v(-175.03, -5.5) * mm, "end": v(-174.98, -5.5) * mm});
            skLineSegment(sketch, "E40.3.0.28", {"start": v(-179.03, -5.5) * mm, "end": v(-178.98, -5.5) * mm});
            skLineSegment(sketch, "E40.3.0.29", {"start": v(-177.03, -1.5) * mm, "end": v(-176.98, -1.5) * mm});
            skLineSegment(sketch, "E40.3.0.30", {"start": v(-181.03, -1.5) * mm, "end": v(-180.98, -1.5) * mm});
            skLineSegment(sketch, "E40.3.0.31", {"start": v(-177.03, -5.5) * mm, "end": v(-176.98, -5.5) * mm});
            skLineSegment(sketch, "E40.3.0.32", {"start": v(-181.03, -5.5) * mm, "end": v(-180.98, -5.5) * mm});
            skLineSegment(sketch, "E40.3.0.33", {"start": v(-183.03, -1.5) * mm, "end": v(-182.98, -1.5) * mm});
            skLineSegment(sketch, "E40.3.0.34", {"start": v(-179.03, -1.5) * mm, "end": v(-178.98, -1.5) * mm});
            skLineSegment(sketch, "E40.3.0.35", {"start": v(-175.03, -1.5) * mm, "end": v(-174.98, -1.5) * mm});
            skLineSegment(sketch, "E40.3.0.36", {"start": v(-183.03, -5.5) * mm, "end": v(-182.98, -5.5) * mm});
            skLineSegment(sketch, "E40.4.0.0", {"start": v(-172.03, -1.5) * mm, "end": v(-172.03, -5.5) * mm});
            skLineSegment(sketch, "E40.4.0.1", {"start": v(-168.03, -1.5) * mm, "end": v(-168.03, -5.5) * mm});
            skLineSegment(sketch, "E40.4.0.2", {"start": v(-173.03, -5.5) * mm, "end": v(-172.03, -5.5) * mm, "construction": true});
            skLineSegment(sketch, "E40.4.0.3", {"start": v(-171.98, -1.5) * mm, "end": v(-171.98, -5.5) * mm});
            skLineSegment(sketch, "E40.4.0.4", {"start": v(-167.98, -1.5) * mm, "end": v(-167.98, -5.5) * mm});
            skLineSegment(sketch, "E40.4.0.5", {"start": v(-172.98, -1.5) * mm, "end": v(-172.98, -5.5) * mm});
            skLineSegment(sketch, "E40.4.0.6", {"start": v(-167.03, -1.5) * mm, "end": v(-167.03, -5.5) * mm});
            skLineSegment(sketch, "E40.4.0.7", {"start": v(-171.03, -1.5) * mm, "end": v(-171.03, -5.5) * mm});
            skLineSegment(sketch, "E40.4.0.8", {"start": v(-169.98, -1.5) * mm, "end": v(-169.98, -5.5) * mm});
            skLineSegment(sketch, "E40.4.0.9", {"start": v(-165.98, -1.5) * mm, "end": v(-165.98, -5.5) * mm});
            skLineSegment(sketch, "E40.4.0.10", {"start": v(-170.03, -1.5) * mm, "end": v(-170.03, -5.5) * mm});
            skLineSegment(sketch, "E40.4.0.11", {"start": v(-166.03, -1.5) * mm, "end": v(-166.03, -5.5) * mm});
            skLineSegment(sketch, "E40.4.0.12", {"start": v(-165.03, -1.5) * mm, "end": v(-165.03, -5.5) * mm});
            skLineSegment(sketch, "E40.4.0.13", {"start": v(-169.03, -1.5) * mm, "end": v(-169.03, -5.5) * mm});
            skLineSegment(sketch, "E40.4.0.14", {"start": v(-166.98, -1.5) * mm, "end": v(-166.98, -5.5) * mm});
            skLineSegment(sketch, "E40.4.0.15", {"start": v(-170.98, -1.5) * mm, "end": v(-170.98, -5.5) * mm});
            skLineSegment(sketch, "E40.4.0.16", {"start": v(-168.98, -1.5) * mm, "end": v(-168.98, -5.5) * mm});
            skLineSegment(sketch, "E40.4.0.17", {"start": v(-164.98, -1.5) * mm, "end": v(-164.98, -5.5) * mm});
            skLineSegment(sketch, "E40.4.0.18", {"start": v(-173.03, -1.5) * mm, "end": v(-173.03, -5.5) * mm});
            skLineSegment(sketch, "E40.4.0.19", {"start": v(-168.03, -5.5) * mm, "end": v(-167.98, -5.5) * mm});
            skLineSegment(sketch, "E40.4.0.20", {"start": v(-172.03, -1.5) * mm, "end": v(-171.98, -1.5) * mm});
            skLineSegment(sketch, "E40.4.0.21", {"start": v(-168.03, -1.5) * mm, "end": v(-167.98, -1.5) * mm});
            skLineSegment(sketch, "E40.4.0.22", {"start": v(-170.03, -1.5) * mm, "end": v(-169.98, -1.5) * mm});
            skLineSegment(sketch, "E40.4.0.23", {"start": v(-166.03, -1.5) * mm, "end": v(-165.98, -1.5) * mm});
            skLineSegment(sketch, "E40.4.0.24", {"start": v(-170.03, -5.5) * mm, "end": v(-169.98, -5.5) * mm});
            skLineSegment(sketch, "E40.4.0.25", {"start": v(-166.03, -5.5) * mm, "end": v(-165.98, -5.5) * mm});
            skLineSegment(sketch, "E40.4.0.26", {"start": v(-172.03, -5.5) * mm, "end": v(-171.98, -5.5) * mm});
            skLineSegment(sketch, "E40.4.0.27", {"start": v(-165.03, -5.5) * mm, "end": v(-164.98, -5.5) * mm});
            skLineSegment(sketch, "E40.4.0.28", {"start": v(-169.03, -5.5) * mm, "end": v(-168.98, -5.5) * mm});
            skLineSegment(sketch, "E40.4.0.29", {"start": v(-167.03, -1.5) * mm, "end": v(-166.98, -1.5) * mm});
            skLineSegment(sketch, "E40.4.0.30", {"start": v(-171.03, -1.5) * mm, "end": v(-170.98, -1.5) * mm});
            skLineSegment(sketch, "E40.4.0.31", {"start": v(-167.03, -5.5) * mm, "end": v(-166.98, -5.5) * mm});
            skLineSegment(sketch, "E40.4.0.32", {"start": v(-171.03, -5.5) * mm, "end": v(-170.98, -5.5) * mm});
            skLineSegment(sketch, "E40.4.0.33", {"start": v(-173.03, -1.5) * mm, "end": v(-172.98, -1.5) * mm});
            skLineSegment(sketch, "E40.4.0.34", {"start": v(-169.03, -1.5) * mm, "end": v(-168.98, -1.5) * mm});
            skLineSegment(sketch, "E40.4.0.35", {"start": v(-165.03, -1.5) * mm, "end": v(-164.98, -1.5) * mm});
            skLineSegment(sketch, "E40.4.0.36", {"start": v(-173.03, -5.5) * mm, "end": v(-172.98, -5.5) * mm});
            skLineSegment(sketch, "E40.5.0.0", {"start": v(-162.03, -1.5) * mm, "end": v(-162.03, -5.5) * mm});
            skLineSegment(sketch, "E40.5.0.1", {"start": v(-158.03, -1.5) * mm, "end": v(-158.03, -5.5) * mm});
            skLineSegment(sketch, "E40.5.0.2", {"start": v(-163.03, -5.5) * mm, "end": v(-162.03, -5.5) * mm, "construction": true});
            skLineSegment(sketch, "E40.5.0.3", {"start": v(-161.98, -1.5) * mm, "end": v(-161.98, -5.5) * mm});
            skLineSegment(sketch, "E40.5.0.4", {"start": v(-157.98, -1.5) * mm, "end": v(-157.98, -5.5) * mm});
            skLineSegment(sketch, "E40.5.0.5", {"start": v(-162.98, -1.5) * mm, "end": v(-162.98, -5.5) * mm});
            skLineSegment(sketch, "E40.5.0.6", {"start": v(-157.03, -1.5) * mm, "end": v(-157.03, -5.5) * mm});
            skLineSegment(sketch, "E40.5.0.7", {"start": v(-161.03, -1.5) * mm, "end": v(-161.03, -5.5) * mm});
            skLineSegment(sketch, "E40.5.0.8", {"start": v(-159.98, -1.5) * mm, "end": v(-159.98, -5.5) * mm});
            skLineSegment(sketch, "E40.5.0.9", {"start": v(-155.98, -1.5) * mm, "end": v(-155.98, -5.5) * mm});
            skLineSegment(sketch, "E40.5.0.10", {"start": v(-160.03, -1.5) * mm, "end": v(-160.03, -5.5) * mm});
            skLineSegment(sketch, "E40.5.0.11", {"start": v(-156.03, -1.5) * mm, "end": v(-156.03, -5.5) * mm});
            skLineSegment(sketch, "E40.5.0.12", {"start": v(-155.03, -1.5) * mm, "end": v(-155.03, -5.5) * mm});
            skLineSegment(sketch, "E40.5.0.13", {"start": v(-159.03, -1.5) * mm, "end": v(-159.03, -5.5) * mm});
            skLineSegment(sketch, "E40.5.0.14", {"start": v(-156.98, -1.5) * mm, "end": v(-156.98, -5.5) * mm});
            skLineSegment(sketch, "E40.5.0.15", {"start": v(-160.98, -1.5) * mm, "end": v(-160.98, -5.5) * mm});
            skLineSegment(sketch, "E40.5.0.16", {"start": v(-158.98, -1.5) * mm, "end": v(-158.98, -5.5) * mm});
            skLineSegment(sketch, "E40.5.0.17", {"start": v(-154.98, -1.5) * mm, "end": v(-154.98, -5.5) * mm});
            skLineSegment(sketch, "E40.5.0.18", {"start": v(-163.03, -1.5) * mm, "end": v(-163.03, -5.5) * mm});
            skLineSegment(sketch, "E40.5.0.19", {"start": v(-158.03, -5.5) * mm, "end": v(-157.98, -5.5) * mm});
            skLineSegment(sketch, "E40.5.0.20", {"start": v(-162.03, -1.5) * mm, "end": v(-161.98, -1.5) * mm});
            skLineSegment(sketch, "E40.5.0.21", {"start": v(-158.03, -1.5) * mm, "end": v(-157.98, -1.5) * mm});
            skLineSegment(sketch, "E40.5.0.22", {"start": v(-160.03, -1.5) * mm, "end": v(-159.98, -1.5) * mm});
            skLineSegment(sketch, "E40.5.0.23", {"start": v(-156.03, -1.5) * mm, "end": v(-155.98, -1.5) * mm});
            skLineSegment(sketch, "E40.5.0.24", {"start": v(-160.03, -5.5) * mm, "end": v(-159.98, -5.5) * mm});
            skLineSegment(sketch, "E40.5.0.25", {"start": v(-156.03, -5.5) * mm, "end": v(-155.98, -5.5) * mm});
            skLineSegment(sketch, "E40.5.0.26", {"start": v(-162.03, -5.5) * mm, "end": v(-161.98, -5.5) * mm});
            skLineSegment(sketch, "E40.5.0.27", {"start": v(-155.03, -5.5) * mm, "end": v(-154.98, -5.5) * mm});
            skLineSegment(sketch, "E40.5.0.28", {"start": v(-159.03, -5.5) * mm, "end": v(-158.98, -5.5) * mm});
            skLineSegment(sketch, "E40.5.0.29", {"start": v(-157.03, -1.5) * mm, "end": v(-156.98, -1.5) * mm});
            skLineSegment(sketch, "E40.5.0.30", {"start": v(-161.03, -1.5) * mm, "end": v(-160.98, -1.5) * mm});
            skLineSegment(sketch, "E40.5.0.31", {"start": v(-157.03, -5.5) * mm, "end": v(-156.98, -5.5) * mm});
            skLineSegment(sketch, "E40.5.0.32", {"start": v(-161.03, -5.5) * mm, "end": v(-160.98, -5.5) * mm});
            skLineSegment(sketch, "E40.5.0.33", {"start": v(-163.03, -1.5) * mm, "end": v(-162.98, -1.5) * mm});
            skLineSegment(sketch, "E40.5.0.34", {"start": v(-159.03, -1.5) * mm, "end": v(-158.98, -1.5) * mm});
            skLineSegment(sketch, "E40.5.0.35", {"start": v(-155.03, -1.5) * mm, "end": v(-154.98, -1.5) * mm});
            skLineSegment(sketch, "E40.5.0.36", {"start": v(-163.03, -5.5) * mm, "end": v(-162.98, -5.5) * mm});
            skLineSegment(sketch, "E40.6.0.0", {"start": v(-152.03, -1.5) * mm, "end": v(-152.03, -5.5) * mm});
            skLineSegment(sketch, "E40.6.0.1", {"start": v(-148.03, -1.5) * mm, "end": v(-148.03, -5.5) * mm});
            skLineSegment(sketch, "E40.6.0.2", {"start": v(-153.03, -5.5) * mm, "end": v(-152.03, -5.5) * mm, "construction": true});
            skLineSegment(sketch, "E40.6.0.3", {"start": v(-151.98, -1.5) * mm, "end": v(-151.98, -5.5) * mm});
            skLineSegment(sketch, "E40.6.0.4", {"start": v(-147.98, -1.5) * mm, "end": v(-147.98, -5.5) * mm});
            skLineSegment(sketch, "E40.6.0.5", {"start": v(-152.98, -1.5) * mm, "end": v(-152.98, -5.5) * mm});
            skLineSegment(sketch, "E40.6.0.6", {"start": v(-147.03, -1.5) * mm, "end": v(-147.03, -5.5) * mm});
            skLineSegment(sketch, "E40.6.0.7", {"start": v(-151.03, -1.5) * mm, "end": v(-151.03, -5.5) * mm});
            skLineSegment(sketch, "E40.6.0.8", {"start": v(-149.98, -1.5) * mm, "end": v(-149.98, -5.5) * mm});
            skLineSegment(sketch, "E40.6.0.9", {"start": v(-145.98, -1.5) * mm, "end": v(-145.98, -5.5) * mm});
            skLineSegment(sketch, "E40.6.0.10", {"start": v(-150.03, -1.5) * mm, "end": v(-150.03, -5.5) * mm});
            skLineSegment(sketch, "E40.6.0.11", {"start": v(-146.03, -1.5) * mm, "end": v(-146.03, -5.5) * mm});
            skLineSegment(sketch, "E40.6.0.12", {"start": v(-145.03, -1.5) * mm, "end": v(-145.03, -5.5) * mm});
            skLineSegment(sketch, "E40.6.0.13", {"start": v(-149.03, -1.5) * mm, "end": v(-149.03, -5.5) * mm});
            skLineSegment(sketch, "E40.6.0.14", {"start": v(-146.98, -1.5) * mm, "end": v(-146.98, -5.5) * mm});
            skLineSegment(sketch, "E40.6.0.15", {"start": v(-150.98, -1.5) * mm, "end": v(-150.98, -5.5) * mm});
            skLineSegment(sketch, "E40.6.0.16", {"start": v(-148.98, -1.5) * mm, "end": v(-148.98, -5.5) * mm});
            skLineSegment(sketch, "E40.6.0.17", {"start": v(-144.98, -1.5) * mm, "end": v(-144.98, -5.5) * mm});
            skLineSegment(sketch, "E40.6.0.18", {"start": v(-153.03, -1.5) * mm, "end": v(-153.03, -5.5) * mm});
            skLineSegment(sketch, "E40.6.0.19", {"start": v(-148.03, -5.5) * mm, "end": v(-147.98, -5.5) * mm});
            skLineSegment(sketch, "E40.6.0.20", {"start": v(-152.03, -1.5) * mm, "end": v(-151.98, -1.5) * mm});
            skLineSegment(sketch, "E40.6.0.21", {"start": v(-148.03, -1.5) * mm, "end": v(-147.98, -1.5) * mm});
            skLineSegment(sketch, "E40.6.0.22", {"start": v(-150.03, -1.5) * mm, "end": v(-149.98, -1.5) * mm});
            skLineSegment(sketch, "E40.6.0.23", {"start": v(-146.03, -1.5) * mm, "end": v(-145.98, -1.5) * mm});
            skLineSegment(sketch, "E40.6.0.24", {"start": v(-150.03, -5.5) * mm, "end": v(-149.98, -5.5) * mm});
            skLineSegment(sketch, "E40.6.0.25", {"start": v(-146.03, -5.5) * mm, "end": v(-145.98, -5.5) * mm});
            skLineSegment(sketch, "E40.6.0.26", {"start": v(-152.03, -5.5) * mm, "end": v(-151.98, -5.5) * mm});
            skLineSegment(sketch, "E40.6.0.27", {"start": v(-145.03, -5.5) * mm, "end": v(-144.98, -5.5) * mm});
            skLineSegment(sketch, "E40.6.0.28", {"start": v(-149.03, -5.5) * mm, "end": v(-148.98, -5.5) * mm});
            skLineSegment(sketch, "E40.6.0.29", {"start": v(-147.03, -1.5) * mm, "end": v(-146.98, -1.5) * mm});
            skLineSegment(sketch, "E40.6.0.30", {"start": v(-151.03, -1.5) * mm, "end": v(-150.98, -1.5) * mm});
            skLineSegment(sketch, "E40.6.0.31", {"start": v(-147.03, -5.5) * mm, "end": v(-146.98, -5.5) * mm});
            skLineSegment(sketch, "E40.6.0.32", {"start": v(-151.03, -5.5) * mm, "end": v(-150.98, -5.5) * mm});
            skLineSegment(sketch, "E40.6.0.33", {"start": v(-153.03, -1.5) * mm, "end": v(-152.98, -1.5) * mm});
            skLineSegment(sketch, "E40.6.0.34", {"start": v(-149.03, -1.5) * mm, "end": v(-148.98, -1.5) * mm});
            skLineSegment(sketch, "E40.6.0.35", {"start": v(-145.03, -1.5) * mm, "end": v(-144.98, -1.5) * mm});
            skLineSegment(sketch, "E40.6.0.36", {"start": v(-153.03, -5.5) * mm, "end": v(-152.98, -5.5) * mm});
            skLineSegment(sketch, "E40.7.0.0", {"start": v(-142.03, -1.5) * mm, "end": v(-142.03, -5.5) * mm});
            skLineSegment(sketch, "E40.7.0.1", {"start": v(-138.03, -1.5) * mm, "end": v(-138.03, -5.5) * mm});
            skLineSegment(sketch, "E40.7.0.2", {"start": v(-143.03, -5.5) * mm, "end": v(-142.03, -5.5) * mm, "construction": true});
            skLineSegment(sketch, "E40.7.0.3", {"start": v(-141.98, -1.5) * mm, "end": v(-141.98, -5.5) * mm});
            skLineSegment(sketch, "E40.7.0.4", {"start": v(-137.98, -1.5) * mm, "end": v(-137.98, -5.5) * mm});
            skLineSegment(sketch, "E40.7.0.5", {"start": v(-142.98, -1.5) * mm, "end": v(-142.98, -5.5) * mm});
            skLineSegment(sketch, "E40.7.0.6", {"start": v(-137.03, -1.5) * mm, "end": v(-137.03, -5.5) * mm});
            skLineSegment(sketch, "E40.7.0.7", {"start": v(-141.03, -1.5) * mm, "end": v(-141.03, -5.5) * mm});
            skLineSegment(sketch, "E40.7.0.8", {"start": v(-139.98, -1.5) * mm, "end": v(-139.98, -5.5) * mm});
            skLineSegment(sketch, "E40.7.0.9", {"start": v(-135.98, -1.5) * mm, "end": v(-135.98, -5.5) * mm});
            skLineSegment(sketch, "E40.7.0.10", {"start": v(-140.03, -1.5) * mm, "end": v(-140.03, -5.5) * mm});
            skLineSegment(sketch, "E40.7.0.11", {"start": v(-136.03, -1.5) * mm, "end": v(-136.03, -5.5) * mm});
            skLineSegment(sketch, "E40.7.0.12", {"start": v(-135.03, -1.5) * mm, "end": v(-135.03, -5.5) * mm});
            skLineSegment(sketch, "E40.7.0.13", {"start": v(-139.03, -1.5) * mm, "end": v(-139.03, -5.5) * mm});
            skLineSegment(sketch, "E40.7.0.14", {"start": v(-136.98, -1.5) * mm, "end": v(-136.98, -5.5) * mm});
            skLineSegment(sketch, "E40.7.0.15", {"start": v(-140.98, -1.5) * mm, "end": v(-140.98, -5.5) * mm});
            skLineSegment(sketch, "E40.7.0.16", {"start": v(-138.98, -1.5) * mm, "end": v(-138.98, -5.5) * mm});
            skLineSegment(sketch, "E40.7.0.17", {"start": v(-134.98, -1.5) * mm, "end": v(-134.98, -5.5) * mm});
            skLineSegment(sketch, "E40.7.0.18", {"start": v(-143.03, -1.5) * mm, "end": v(-143.03, -5.5) * mm});
            skLineSegment(sketch, "E40.7.0.19", {"start": v(-138.03, -5.5) * mm, "end": v(-137.98, -5.5) * mm});
            skLineSegment(sketch, "E40.7.0.20", {"start": v(-142.03, -1.5) * mm, "end": v(-141.98, -1.5) * mm});
            skLineSegment(sketch, "E40.7.0.21", {"start": v(-138.03, -1.5) * mm, "end": v(-137.98, -1.5) * mm});
            skLineSegment(sketch, "E40.7.0.22", {"start": v(-140.03, -1.5) * mm, "end": v(-139.98, -1.5) * mm});
            skLineSegment(sketch, "E40.7.0.23", {"start": v(-136.03, -1.5) * mm, "end": v(-135.98, -1.5) * mm});
            skLineSegment(sketch, "E40.7.0.24", {"start": v(-140.03, -5.5) * mm, "end": v(-139.98, -5.5) * mm});
            skLineSegment(sketch, "E40.7.0.25", {"start": v(-136.03, -5.5) * mm, "end": v(-135.98, -5.5) * mm});
            skLineSegment(sketch, "E40.7.0.26", {"start": v(-142.03, -5.5) * mm, "end": v(-141.98, -5.5) * mm});
            skLineSegment(sketch, "E40.7.0.27", {"start": v(-135.03, -5.5) * mm, "end": v(-134.98, -5.5) * mm});
            skLineSegment(sketch, "E40.7.0.28", {"start": v(-139.03, -5.5) * mm, "end": v(-138.98, -5.5) * mm});
            skLineSegment(sketch, "E40.7.0.29", {"start": v(-137.03, -1.5) * mm, "end": v(-136.98, -1.5) * mm});
            skLineSegment(sketch, "E40.7.0.30", {"start": v(-141.03, -1.5) * mm, "end": v(-140.98, -1.5) * mm});
            skLineSegment(sketch, "E40.7.0.31", {"start": v(-137.03, -5.5) * mm, "end": v(-136.98, -5.5) * mm});
            skLineSegment(sketch, "E40.7.0.32", {"start": v(-141.03, -5.5) * mm, "end": v(-140.98, -5.5) * mm});
            skLineSegment(sketch, "E40.7.0.33", {"start": v(-143.03, -1.5) * mm, "end": v(-142.98, -1.5) * mm});
            skLineSegment(sketch, "E40.7.0.34", {"start": v(-139.03, -1.5) * mm, "end": v(-138.98, -1.5) * mm});
            skLineSegment(sketch, "E40.7.0.35", {"start": v(-135.03, -1.5) * mm, "end": v(-134.98, -1.5) * mm});
            skLineSegment(sketch, "E40.7.0.36", {"start": v(-143.03, -5.5) * mm, "end": v(-142.98, -5.5) * mm});
            skLineSegment(sketch, "E40.8.0.0", {"start": v(-132.03, -1.5) * mm, "end": v(-132.03, -5.5) * mm});
            skLineSegment(sketch, "E40.8.0.1", {"start": v(-128.03, -1.5) * mm, "end": v(-128.03, -5.5) * mm});
            skLineSegment(sketch, "E40.8.0.2", {"start": v(-133.03, -5.5) * mm, "end": v(-132.03, -5.5) * mm, "construction": true});
            skLineSegment(sketch, "E40.8.0.3", {"start": v(-131.98, -1.5) * mm, "end": v(-131.98, -5.5) * mm});
            skLineSegment(sketch, "E40.8.0.4", {"start": v(-127.98, -1.5) * mm, "end": v(-127.98, -5.5) * mm});
            skLineSegment(sketch, "E40.8.0.5", {"start": v(-132.98, -1.5) * mm, "end": v(-132.98, -5.5) * mm});
            skLineSegment(sketch, "E40.8.0.6", {"start": v(-127.03, -1.5) * mm, "end": v(-127.03, -5.5) * mm});
            skLineSegment(sketch, "E40.8.0.7", {"start": v(-131.03, -1.5) * mm, "end": v(-131.03, -5.5) * mm});
            skLineSegment(sketch, "E40.8.0.8", {"start": v(-129.98, -1.5) * mm, "end": v(-129.98, -5.5) * mm});
            skLineSegment(sketch, "E40.8.0.9", {"start": v(-125.98, -1.5) * mm, "end": v(-125.98, -5.5) * mm});
            skLineSegment(sketch, "E40.8.0.10", {"start": v(-130.03, -1.5) * mm, "end": v(-130.03, -5.5) * mm});
            skLineSegment(sketch, "E40.8.0.11", {"start": v(-126.03, -1.5) * mm, "end": v(-126.03, -5.5) * mm});
            skLineSegment(sketch, "E40.8.0.12", {"start": v(-125.03, -1.5) * mm, "end": v(-125.03, -5.5) * mm});
            skLineSegment(sketch, "E40.8.0.13", {"start": v(-129.03, -1.5) * mm, "end": v(-129.03, -5.5) * mm});
            skLineSegment(sketch, "E40.8.0.14", {"start": v(-126.98, -1.5) * mm, "end": v(-126.98, -5.5) * mm});
            skLineSegment(sketch, "E40.8.0.15", {"start": v(-130.98, -1.5) * mm, "end": v(-130.98, -5.5) * mm});
            skLineSegment(sketch, "E40.8.0.16", {"start": v(-128.98, -1.5) * mm, "end": v(-128.98, -5.5) * mm});
            skLineSegment(sketch, "E40.8.0.17", {"start": v(-124.98, -1.5) * mm, "end": v(-124.98, -5.5) * mm});
            skLineSegment(sketch, "E40.8.0.18", {"start": v(-133.03, -1.5) * mm, "end": v(-133.03, -5.5) * mm});
            skLineSegment(sketch, "E40.8.0.19", {"start": v(-128.03, -5.5) * mm, "end": v(-127.98, -5.5) * mm});
            skLineSegment(sketch, "E40.8.0.20", {"start": v(-132.03, -1.5) * mm, "end": v(-131.98, -1.5) * mm});
            skLineSegment(sketch, "E40.8.0.21", {"start": v(-128.03, -1.5) * mm, "end": v(-127.98, -1.5) * mm});
            skLineSegment(sketch, "E40.8.0.22", {"start": v(-130.03, -1.5) * mm, "end": v(-129.98, -1.5) * mm});
            skLineSegment(sketch, "E40.8.0.23", {"start": v(-126.03, -1.5) * mm, "end": v(-125.98, -1.5) * mm});
            skLineSegment(sketch, "E40.8.0.24", {"start": v(-130.03, -5.5) * mm, "end": v(-129.98, -5.5) * mm});
            skLineSegment(sketch, "E40.8.0.25", {"start": v(-126.03, -5.5) * mm, "end": v(-125.98, -5.5) * mm});
            skLineSegment(sketch, "E40.8.0.26", {"start": v(-132.03, -5.5) * mm, "end": v(-131.98, -5.5) * mm});
            skLineSegment(sketch, "E40.8.0.27", {"start": v(-125.03, -5.5) * mm, "end": v(-124.98, -5.5) * mm});
            skLineSegment(sketch, "E40.8.0.28", {"start": v(-129.03, -5.5) * mm, "end": v(-128.98, -5.5) * mm});
            skLineSegment(sketch, "E40.8.0.29", {"start": v(-127.03, -1.5) * mm, "end": v(-126.98, -1.5) * mm});
            skLineSegment(sketch, "E40.8.0.30", {"start": v(-131.03, -1.5) * mm, "end": v(-130.98, -1.5) * mm});
            skLineSegment(sketch, "E40.8.0.31", {"start": v(-127.03, -5.5) * mm, "end": v(-126.98, -5.5) * mm});
            skLineSegment(sketch, "E40.8.0.32", {"start": v(-131.03, -5.5) * mm, "end": v(-130.98, -5.5) * mm});
            skLineSegment(sketch, "E40.8.0.33", {"start": v(-133.03, -1.5) * mm, "end": v(-132.98, -1.5) * mm});
            skLineSegment(sketch, "E40.8.0.34", {"start": v(-129.03, -1.5) * mm, "end": v(-128.98, -1.5) * mm});
            skLineSegment(sketch, "E40.8.0.35", {"start": v(-125.03, -1.5) * mm, "end": v(-124.98, -1.5) * mm});
            skLineSegment(sketch, "E40.8.0.36", {"start": v(-133.03, -5.5) * mm, "end": v(-132.98, -5.5) * mm});
            skLineSegment(sketch, "E40.9.0.0", {"start": v(-122.03, -1.5) * mm, "end": v(-122.03, -5.5) * mm});
            skLineSegment(sketch, "E40.9.0.1", {"start": v(-118.03, -1.5) * mm, "end": v(-118.03, -5.5) * mm});
            skLineSegment(sketch, "E40.9.0.2", {"start": v(-123.03, -5.5) * mm, "end": v(-122.03, -5.5) * mm, "construction": true});
            skLineSegment(sketch, "E40.9.0.3", {"start": v(-121.98, -1.5) * mm, "end": v(-121.98, -5.5) * mm});
            skLineSegment(sketch, "E40.9.0.4", {"start": v(-117.98, -1.5) * mm, "end": v(-117.98, -5.5) * mm});
            skLineSegment(sketch, "E40.9.0.5", {"start": v(-122.98, -1.5) * mm, "end": v(-122.98, -5.5) * mm});
            skLineSegment(sketch, "E40.9.0.6", {"start": v(-117.03, -1.5) * mm, "end": v(-117.03, -5.5) * mm});
            skLineSegment(sketch, "E40.9.0.7", {"start": v(-121.03, -1.5) * mm, "end": v(-121.03, -5.5) * mm});
            skLineSegment(sketch, "E40.9.0.8", {"start": v(-119.98, -1.5) * mm, "end": v(-119.98, -5.5) * mm});
            skLineSegment(sketch, "E40.9.0.9", {"start": v(-115.98, -1.5) * mm, "end": v(-115.98, -5.5) * mm});
            skLineSegment(sketch, "E40.9.0.10", {"start": v(-120.03, -1.5) * mm, "end": v(-120.03, -5.5) * mm});
            skLineSegment(sketch, "E40.9.0.11", {"start": v(-116.03, -1.5) * mm, "end": v(-116.03, -5.5) * mm});
            skLineSegment(sketch, "E40.9.0.12", {"start": v(-115.03, -1.5) * mm, "end": v(-115.03, -5.5) * mm});
            skLineSegment(sketch, "E40.9.0.13", {"start": v(-119.03, -1.5) * mm, "end": v(-119.03, -5.5) * mm});
            skLineSegment(sketch, "E40.9.0.14", {"start": v(-116.98, -1.5) * mm, "end": v(-116.98, -5.5) * mm});
            skLineSegment(sketch, "E40.9.0.15", {"start": v(-120.98, -1.5) * mm, "end": v(-120.98, -5.5) * mm});
            skLineSegment(sketch, "E40.9.0.16", {"start": v(-118.98, -1.5) * mm, "end": v(-118.98, -5.5) * mm});
            skLineSegment(sketch, "E40.9.0.17", {"start": v(-114.98, -1.5) * mm, "end": v(-114.98, -5.5) * mm});
            skLineSegment(sketch, "E40.9.0.18", {"start": v(-123.03, -1.5) * mm, "end": v(-123.03, -5.5) * mm});
            skLineSegment(sketch, "E40.9.0.19", {"start": v(-118.03, -5.5) * mm, "end": v(-117.98, -5.5) * mm});
            skLineSegment(sketch, "E40.9.0.20", {"start": v(-122.03, -1.5) * mm, "end": v(-121.98, -1.5) * mm});
            skLineSegment(sketch, "E40.9.0.21", {"start": v(-118.03, -1.5) * mm, "end": v(-117.98, -1.5) * mm});
            skLineSegment(sketch, "E40.9.0.22", {"start": v(-120.03, -1.5) * mm, "end": v(-119.98, -1.5) * mm});
            skLineSegment(sketch, "E40.9.0.23", {"start": v(-116.03, -1.5) * mm, "end": v(-115.98, -1.5) * mm});
            skLineSegment(sketch, "E40.9.0.24", {"start": v(-120.03, -5.5) * mm, "end": v(-119.98, -5.5) * mm});
            skLineSegment(sketch, "E40.9.0.25", {"start": v(-116.03, -5.5) * mm, "end": v(-115.98, -5.5) * mm});
            skLineSegment(sketch, "E40.9.0.26", {"start": v(-122.03, -5.5) * mm, "end": v(-121.98, -5.5) * mm});
            skLineSegment(sketch, "E40.9.0.27", {"start": v(-115.03, -5.5) * mm, "end": v(-114.98, -5.5) * mm});
            skLineSegment(sketch, "E40.9.0.28", {"start": v(-119.03, -5.5) * mm, "end": v(-118.98, -5.5) * mm});
            skLineSegment(sketch, "E40.9.0.29", {"start": v(-117.03, -1.5) * mm, "end": v(-116.98, -1.5) * mm});
            skLineSegment(sketch, "E40.9.0.30", {"start": v(-121.03, -1.5) * mm, "end": v(-120.98, -1.5) * mm});
            skLineSegment(sketch, "E40.9.0.31", {"start": v(-117.03, -5.5) * mm, "end": v(-116.98, -5.5) * mm});
            skLineSegment(sketch, "E40.9.0.32", {"start": v(-121.03, -5.5) * mm, "end": v(-120.98, -5.5) * mm});
            skLineSegment(sketch, "E40.9.0.33", {"start": v(-123.03, -1.5) * mm, "end": v(-122.98, -1.5) * mm});
            skLineSegment(sketch, "E40.9.0.34", {"start": v(-119.03, -1.5) * mm, "end": v(-118.98, -1.5) * mm});
            skLineSegment(sketch, "E40.9.0.35", {"start": v(-115.03, -1.5) * mm, "end": v(-114.98, -1.5) * mm});
            skLineSegment(sketch, "E40.9.0.36", {"start": v(-123.03, -5.5) * mm, "end": v(-122.98, -5.5) * mm});
            skLineSegment(sketch, "E40.10.0.0", {"start": v(-112.03, -1.5) * mm, "end": v(-112.03, -5.5) * mm});
            skLineSegment(sketch, "E40.10.0.1", {"start": v(-108.03, -1.5) * mm, "end": v(-108.03, -5.5) * mm});
            skLineSegment(sketch, "E40.10.0.2", {"start": v(-113.03, -5.5) * mm, "end": v(-112.03, -5.5) * mm, "construction": true});
            skLineSegment(sketch, "E40.10.0.3", {"start": v(-111.98, -1.5) * mm, "end": v(-111.98, -5.5) * mm});
            skLineSegment(sketch, "E40.10.0.4", {"start": v(-107.98, -1.5) * mm, "end": v(-107.98, -5.5) * mm});
            skLineSegment(sketch, "E40.10.0.5", {"start": v(-112.98, -1.5) * mm, "end": v(-112.98, -5.5) * mm});
            skLineSegment(sketch, "E40.10.0.6", {"start": v(-107.03, -1.5) * mm, "end": v(-107.03, -5.5) * mm});
            skLineSegment(sketch, "E40.10.0.7", {"start": v(-111.03, -1.5) * mm, "end": v(-111.03, -5.5) * mm});
            skLineSegment(sketch, "E40.10.0.8", {"start": v(-109.98, -1.5) * mm, "end": v(-109.98, -5.5) * mm});
            skLineSegment(sketch, "E40.10.0.9", {"start": v(-105.98, -1.5) * mm, "end": v(-105.98, -5.5) * mm});
            skLineSegment(sketch, "E40.10.0.10", {"start": v(-110.03, -1.5) * mm, "end": v(-110.03, -5.5) * mm});
            skLineSegment(sketch, "E40.10.0.11", {"start": v(-106.03, -1.5) * mm, "end": v(-106.03, -5.5) * mm});
            skLineSegment(sketch, "E40.10.0.12", {"start": v(-105.03, -1.5) * mm, "end": v(-105.03, -5.5) * mm});
            skLineSegment(sketch, "E40.10.0.13", {"start": v(-109.03, -1.5) * mm, "end": v(-109.03, -5.5) * mm});
            skLineSegment(sketch, "E40.10.0.14", {"start": v(-106.98, -1.5) * mm, "end": v(-106.98, -5.5) * mm});
            skLineSegment(sketch, "E40.10.0.15", {"start": v(-110.98, -1.5) * mm, "end": v(-110.98, -5.5) * mm});
            skLineSegment(sketch, "E40.10.0.16", {"start": v(-108.98, -1.5) * mm, "end": v(-108.98, -5.5) * mm});
            skLineSegment(sketch, "E40.10.0.17", {"start": v(-104.98, -1.5) * mm, "end": v(-104.98, -5.5) * mm});
            skLineSegment(sketch, "E40.10.0.18", {"start": v(-113.03, -1.5) * mm, "end": v(-113.03, -5.5) * mm});
            skLineSegment(sketch, "E40.10.0.19", {"start": v(-108.03, -5.5) * mm, "end": v(-107.98, -5.5) * mm});
            skLineSegment(sketch, "E40.10.0.20", {"start": v(-112.03, -1.5) * mm, "end": v(-111.98, -1.5) * mm});
            skLineSegment(sketch, "E40.10.0.21", {"start": v(-108.03, -1.5) * mm, "end": v(-107.98, -1.5) * mm});
            skLineSegment(sketch, "E40.10.0.22", {"start": v(-110.03, -1.5) * mm, "end": v(-109.98, -1.5) * mm});
            skLineSegment(sketch, "E40.10.0.23", {"start": v(-106.03, -1.5) * mm, "end": v(-105.98, -1.5) * mm});
            skLineSegment(sketch, "E40.10.0.24", {"start": v(-110.03, -5.5) * mm, "end": v(-109.98, -5.5) * mm});
            skLineSegment(sketch, "E40.10.0.25", {"start": v(-106.03, -5.5) * mm, "end": v(-105.98, -5.5) * mm});
            skLineSegment(sketch, "E40.10.0.26", {"start": v(-112.03, -5.5) * mm, "end": v(-111.98, -5.5) * mm});
            skLineSegment(sketch, "E40.10.0.27", {"start": v(-105.03, -5.5) * mm, "end": v(-104.98, -5.5) * mm});
            skLineSegment(sketch, "E40.10.0.28", {"start": v(-109.03, -5.5) * mm, "end": v(-108.98, -5.5) * mm});
            skLineSegment(sketch, "E40.10.0.29", {"start": v(-107.03, -1.5) * mm, "end": v(-106.98, -1.5) * mm});
            skLineSegment(sketch, "E40.10.0.30", {"start": v(-111.03, -1.5) * mm, "end": v(-110.98, -1.5) * mm});
            skLineSegment(sketch, "E40.10.0.31", {"start": v(-107.03, -5.5) * mm, "end": v(-106.98, -5.5) * mm});
            skLineSegment(sketch, "E40.10.0.32", {"start": v(-111.03, -5.5) * mm, "end": v(-110.98, -5.5) * mm});
            skLineSegment(sketch, "E40.10.0.33", {"start": v(-113.03, -1.5) * mm, "end": v(-112.98, -1.5) * mm});
            skLineSegment(sketch, "E40.10.0.34", {"start": v(-109.03, -1.5) * mm, "end": v(-108.98, -1.5) * mm});
            skLineSegment(sketch, "E40.10.0.35", {"start": v(-105.03, -1.5) * mm, "end": v(-104.98, -1.5) * mm});
            skLineSegment(sketch, "E40.10.0.36", {"start": v(-113.03, -5.5) * mm, "end": v(-112.98, -5.5) * mm});
            skLineSegment(sketch, "E40.11.0.0", {"start": v(-102.03, -1.5) * mm, "end": v(-102.03, -5.5) * mm});
            skLineSegment(sketch, "E40.11.0.1", {"start": v(-98.03, -1.5) * mm, "end": v(-98.03, -5.5) * mm});
            skLineSegment(sketch, "E40.11.0.2", {"start": v(-103.03, -5.5) * mm, "end": v(-102.03, -5.5) * mm, "construction": true});
            skLineSegment(sketch, "E40.11.0.3", {"start": v(-101.98, -1.5) * mm, "end": v(-101.98, -5.5) * mm});
            skLineSegment(sketch, "E40.11.0.4", {"start": v(-97.98, -1.5) * mm, "end": v(-97.98, -5.5) * mm});
            skLineSegment(sketch, "E40.11.0.5", {"start": v(-102.98, -1.5) * mm, "end": v(-102.98, -5.5) * mm});
            skLineSegment(sketch, "E40.11.0.6", {"start": v(-97.03, -1.5) * mm, "end": v(-97.03, -5.5) * mm});
            skLineSegment(sketch, "E40.11.0.7", {"start": v(-101.03, -1.5) * mm, "end": v(-101.03, -5.5) * mm});
            skLineSegment(sketch, "E40.11.0.8", {"start": v(-99.98, -1.5) * mm, "end": v(-99.98, -5.5) * mm});
            skLineSegment(sketch, "E40.11.0.9", {"start": v(-95.98, -1.5) * mm, "end": v(-95.98, -5.5) * mm});
            skLineSegment(sketch, "E40.11.0.10", {"start": v(-100.03, -1.5) * mm, "end": v(-100.03, -5.5) * mm});
            skLineSegment(sketch, "E40.11.0.11", {"start": v(-96.03, -1.5) * mm, "end": v(-96.03, -5.5) * mm});
            skLineSegment(sketch, "E40.11.0.12", {"start": v(-95.03, -1.5) * mm, "end": v(-95.03, -5.5) * mm});
            skLineSegment(sketch, "E40.11.0.13", {"start": v(-99.03, -1.5) * mm, "end": v(-99.03, -5.5) * mm});
            skLineSegment(sketch, "E40.11.0.14", {"start": v(-96.98, -1.5) * mm, "end": v(-96.98, -5.5) * mm});
            skLineSegment(sketch, "E40.11.0.15", {"start": v(-100.98, -1.5) * mm, "end": v(-100.98, -5.5) * mm});
            skLineSegment(sketch, "E40.11.0.16", {"start": v(-98.98, -1.5) * mm, "end": v(-98.98, -5.5) * mm});
            skLineSegment(sketch, "E40.11.0.17", {"start": v(-94.98, -1.5) * mm, "end": v(-94.98, -5.5) * mm});
            skLineSegment(sketch, "E40.11.0.18", {"start": v(-103.03, -1.5) * mm, "end": v(-103.03, -5.5) * mm});
            skLineSegment(sketch, "E40.11.0.19", {"start": v(-98.03, -5.5) * mm, "end": v(-97.98, -5.5) * mm});
            skLineSegment(sketch, "E40.11.0.20", {"start": v(-102.03, -1.5) * mm, "end": v(-101.98, -1.5) * mm});
            skLineSegment(sketch, "E40.11.0.21", {"start": v(-98.03, -1.5) * mm, "end": v(-97.98, -1.5) * mm});
            skLineSegment(sketch, "E40.11.0.22", {"start": v(-100.03, -1.5) * mm, "end": v(-99.98, -1.5) * mm});
            skLineSegment(sketch, "E40.11.0.23", {"start": v(-96.03, -1.5) * mm, "end": v(-95.98, -1.5) * mm});
            skLineSegment(sketch, "E40.11.0.24", {"start": v(-100.03, -5.5) * mm, "end": v(-99.98, -5.5) * mm});
            skLineSegment(sketch, "E40.11.0.25", {"start": v(-96.03, -5.5) * mm, "end": v(-95.98, -5.5) * mm});
            skLineSegment(sketch, "E40.11.0.26", {"start": v(-102.03, -5.5) * mm, "end": v(-101.98, -5.5) * mm});
            skLineSegment(sketch, "E40.11.0.27", {"start": v(-95.03, -5.5) * mm, "end": v(-94.98, -5.5) * mm});
            skLineSegment(sketch, "E40.11.0.28", {"start": v(-99.03, -5.5) * mm, "end": v(-98.98, -5.5) * mm});
            skLineSegment(sketch, "E40.11.0.29", {"start": v(-97.03, -1.5) * mm, "end": v(-96.98, -1.5) * mm});
            skLineSegment(sketch, "E40.11.0.30", {"start": v(-101.03, -1.5) * mm, "end": v(-100.98, -1.5) * mm});
            skLineSegment(sketch, "E40.11.0.31", {"start": v(-97.03, -5.5) * mm, "end": v(-96.98, -5.5) * mm});
            skLineSegment(sketch, "E40.11.0.32", {"start": v(-101.03, -5.5) * mm, "end": v(-100.98, -5.5) * mm});
            skLineSegment(sketch, "E40.11.0.33", {"start": v(-103.03, -1.5) * mm, "end": v(-102.98, -1.5) * mm});
            skLineSegment(sketch, "E40.11.0.34", {"start": v(-99.03, -1.5) * mm, "end": v(-98.98, -1.5) * mm});
            skLineSegment(sketch, "E40.11.0.35", {"start": v(-95.03, -1.5) * mm, "end": v(-94.98, -1.5) * mm});
            skLineSegment(sketch, "E40.11.0.36", {"start": v(-103.03, -5.5) * mm, "end": v(-102.98, -5.5) * mm});
            skLineSegment(sketch, "E40.12.0.0", {"start": v(-92.03, -1.5) * mm, "end": v(-92.03, -5.5) * mm});
            skLineSegment(sketch, "E40.12.0.1", {"start": v(-88.03, -1.5) * mm, "end": v(-88.03, -5.5) * mm});
            skLineSegment(sketch, "E40.12.0.2", {"start": v(-93.03, -5.5) * mm, "end": v(-92.03, -5.5) * mm, "construction": true});
            skLineSegment(sketch, "E40.12.0.3", {"start": v(-91.98, -1.5) * mm, "end": v(-91.98, -5.5) * mm});
            skLineSegment(sketch, "E40.12.0.4", {"start": v(-87.98, -1.5) * mm, "end": v(-87.98, -5.5) * mm});
            skLineSegment(sketch, "E40.12.0.5", {"start": v(-92.98, -1.5) * mm, "end": v(-92.98, -5.5) * mm});
            skLineSegment(sketch, "E40.12.0.6", {"start": v(-87.03, -1.5) * mm, "end": v(-87.03, -5.5) * mm});
            skLineSegment(sketch, "E40.12.0.7", {"start": v(-91.03, -1.5) * mm, "end": v(-91.03, -5.5) * mm});
            skLineSegment(sketch, "E40.12.0.8", {"start": v(-89.98, -1.5) * mm, "end": v(-89.98, -5.5) * mm});
            skLineSegment(sketch, "E40.12.0.9", {"start": v(-85.98, -1.5) * mm, "end": v(-85.98, -5.5) * mm});
            skLineSegment(sketch, "E40.12.0.10", {"start": v(-90.03, -1.5) * mm, "end": v(-90.03, -5.5) * mm});
            skLineSegment(sketch, "E40.12.0.11", {"start": v(-86.03, -1.5) * mm, "end": v(-86.03, -5.5) * mm});
            skLineSegment(sketch, "E40.12.0.12", {"start": v(-85.03, -1.5) * mm, "end": v(-85.03, -5.5) * mm});
            skLineSegment(sketch, "E40.12.0.13", {"start": v(-89.03, -1.5) * mm, "end": v(-89.03, -5.5) * mm});
            skLineSegment(sketch, "E40.12.0.14", {"start": v(-86.98, -1.5) * mm, "end": v(-86.98, -5.5) * mm});
            skLineSegment(sketch, "E40.12.0.15", {"start": v(-90.98, -1.5) * mm, "end": v(-90.98, -5.5) * mm});
            skLineSegment(sketch, "E40.12.0.16", {"start": v(-88.98, -1.5) * mm, "end": v(-88.98, -5.5) * mm});
            skLineSegment(sketch, "E40.12.0.17", {"start": v(-84.98, -1.5) * mm, "end": v(-84.98, -5.5) * mm});
            skLineSegment(sketch, "E40.12.0.18", {"start": v(-93.03, -1.5) * mm, "end": v(-93.03, -5.5) * mm});
            skLineSegment(sketch, "E40.12.0.19", {"start": v(-88.03, -5.5) * mm, "end": v(-87.98, -5.5) * mm});
            skLineSegment(sketch, "E40.12.0.20", {"start": v(-92.03, -1.5) * mm, "end": v(-91.98, -1.5) * mm});
            skLineSegment(sketch, "E40.12.0.21", {"start": v(-88.03, -1.5) * mm, "end": v(-87.98, -1.5) * mm});
            skLineSegment(sketch, "E40.12.0.22", {"start": v(-90.03, -1.5) * mm, "end": v(-89.98, -1.5) * mm});
            skLineSegment(sketch, "E40.12.0.23", {"start": v(-86.03, -1.5) * mm, "end": v(-85.98, -1.5) * mm});
            skLineSegment(sketch, "E40.12.0.24", {"start": v(-90.03, -5.5) * mm, "end": v(-89.98, -5.5) * mm});
            skLineSegment(sketch, "E40.12.0.25", {"start": v(-86.03, -5.5) * mm, "end": v(-85.98, -5.5) * mm});
            skLineSegment(sketch, "E40.12.0.26", {"start": v(-92.03, -5.5) * mm, "end": v(-91.98, -5.5) * mm});
            skLineSegment(sketch, "E40.12.0.27", {"start": v(-85.03, -5.5) * mm, "end": v(-84.98, -5.5) * mm});
            skLineSegment(sketch, "E40.12.0.28", {"start": v(-89.03, -5.5) * mm, "end": v(-88.98, -5.5) * mm});
            skLineSegment(sketch, "E40.12.0.29", {"start": v(-87.03, -1.5) * mm, "end": v(-86.98, -1.5) * mm});
            skLineSegment(sketch, "E40.12.0.30", {"start": v(-91.03, -1.5) * mm, "end": v(-90.98, -1.5) * mm});
            skLineSegment(sketch, "E40.12.0.31", {"start": v(-87.03, -5.5) * mm, "end": v(-86.98, -5.5) * mm});
            skLineSegment(sketch, "E40.12.0.32", {"start": v(-91.03, -5.5) * mm, "end": v(-90.98, -5.5) * mm});
            skLineSegment(sketch, "E40.12.0.33", {"start": v(-93.03, -1.5) * mm, "end": v(-92.98, -1.5) * mm});
            skLineSegment(sketch, "E40.12.0.34", {"start": v(-89.03, -1.5) * mm, "end": v(-88.98, -1.5) * mm});
            skLineSegment(sketch, "E40.12.0.35", {"start": v(-85.03, -1.5) * mm, "end": v(-84.98, -1.5) * mm});
            skLineSegment(sketch, "E40.12.0.36", {"start": v(-93.03, -5.5) * mm, "end": v(-92.98, -5.5) * mm});
            skLineSegment(sketch, "E40.13.0.0", {"start": v(-82.03, -1.5) * mm, "end": v(-82.03, -5.5) * mm});
            skLineSegment(sketch, "E40.13.0.1", {"start": v(-78.03, -1.5) * mm, "end": v(-78.03, -5.5) * mm});
            skLineSegment(sketch, "E40.13.0.2", {"start": v(-83.03, -5.5) * mm, "end": v(-82.03, -5.5) * mm, "construction": true});
            skLineSegment(sketch, "E40.13.0.3", {"start": v(-81.98, -1.5) * mm, "end": v(-81.98, -5.5) * mm});
            skLineSegment(sketch, "E40.13.0.4", {"start": v(-77.98, -1.5) * mm, "end": v(-77.98, -5.5) * mm});
            skLineSegment(sketch, "E40.13.0.5", {"start": v(-82.98, -1.5) * mm, "end": v(-82.98, -5.5) * mm});
            skLineSegment(sketch, "E40.13.0.6", {"start": v(-77.03, -1.5) * mm, "end": v(-77.03, -5.5) * mm});
            skLineSegment(sketch, "E40.13.0.7", {"start": v(-81.03, -1.5) * mm, "end": v(-81.03, -5.5) * mm});
            skLineSegment(sketch, "E40.13.0.8", {"start": v(-79.98, -1.5) * mm, "end": v(-79.98, -5.5) * mm});
            skLineSegment(sketch, "E40.13.0.9", {"start": v(-75.98, -1.5) * mm, "end": v(-75.98, -5.5) * mm});
            skLineSegment(sketch, "E40.13.0.10", {"start": v(-80.03, -1.5) * mm, "end": v(-80.03, -5.5) * mm});
            skLineSegment(sketch, "E40.13.0.11", {"start": v(-76.03, -1.5) * mm, "end": v(-76.03, -5.5) * mm});
            skLineSegment(sketch, "E40.13.0.12", {"start": v(-75.03, -1.5) * mm, "end": v(-75.03, -5.5) * mm});
            skLineSegment(sketch, "E40.13.0.13", {"start": v(-79.03, -1.5) * mm, "end": v(-79.03, -5.5) * mm});
            skLineSegment(sketch, "E40.13.0.14", {"start": v(-76.98, -1.5) * mm, "end": v(-76.98, -5.5) * mm});
            skLineSegment(sketch, "E40.13.0.15", {"start": v(-80.98, -1.5) * mm, "end": v(-80.98, -5.5) * mm});
            skLineSegment(sketch, "E40.13.0.16", {"start": v(-78.98, -1.5) * mm, "end": v(-78.98, -5.5) * mm});
            skLineSegment(sketch, "E40.13.0.17", {"start": v(-74.98, -1.5) * mm, "end": v(-74.98, -5.5) * mm});
            skLineSegment(sketch, "E40.13.0.18", {"start": v(-83.03, -1.5) * mm, "end": v(-83.03, -5.5) * mm});
            skLineSegment(sketch, "E40.13.0.19", {"start": v(-78.03, -5.5) * mm, "end": v(-77.98, -5.5) * mm});
            skLineSegment(sketch, "E40.13.0.20", {"start": v(-82.03, -1.5) * mm, "end": v(-81.98, -1.5) * mm});
            skLineSegment(sketch, "E40.13.0.21", {"start": v(-78.03, -1.5) * mm, "end": v(-77.98, -1.5) * mm});
            skLineSegment(sketch, "E40.13.0.22", {"start": v(-80.03, -1.5) * mm, "end": v(-79.98, -1.5) * mm});
            skLineSegment(sketch, "E40.13.0.23", {"start": v(-76.03, -1.5) * mm, "end": v(-75.98, -1.5) * mm});
            skLineSegment(sketch, "E40.13.0.24", {"start": v(-80.03, -5.5) * mm, "end": v(-79.98, -5.5) * mm});
            skLineSegment(sketch, "E40.13.0.25", {"start": v(-76.03, -5.5) * mm, "end": v(-75.98, -5.5) * mm});
            skLineSegment(sketch, "E40.13.0.26", {"start": v(-82.03, -5.5) * mm, "end": v(-81.98, -5.5) * mm});
            skLineSegment(sketch, "E40.13.0.27", {"start": v(-75.03, -5.5) * mm, "end": v(-74.98, -5.5) * mm});
            skLineSegment(sketch, "E40.13.0.28", {"start": v(-79.03, -5.5) * mm, "end": v(-78.98, -5.5) * mm});
            skLineSegment(sketch, "E40.13.0.29", {"start": v(-77.03, -1.5) * mm, "end": v(-76.98, -1.5) * mm});
            skLineSegment(sketch, "E40.13.0.30", {"start": v(-81.03, -1.5) * mm, "end": v(-80.98, -1.5) * mm});
            skLineSegment(sketch, "E40.13.0.31", {"start": v(-77.03, -5.5) * mm, "end": v(-76.98, -5.5) * mm});
            skLineSegment(sketch, "E40.13.0.32", {"start": v(-81.03, -5.5) * mm, "end": v(-80.98, -5.5) * mm});
            skLineSegment(sketch, "E40.13.0.33", {"start": v(-83.03, -1.5) * mm, "end": v(-82.98, -1.5) * mm});
            skLineSegment(sketch, "E40.13.0.34", {"start": v(-79.03, -1.5) * mm, "end": v(-78.98, -1.5) * mm});
            skLineSegment(sketch, "E40.13.0.35", {"start": v(-75.03, -1.5) * mm, "end": v(-74.98, -1.5) * mm});
            skLineSegment(sketch, "E40.13.0.36", {"start": v(-83.03, -5.5) * mm, "end": v(-82.98, -5.5) * mm});
            skLineSegment(sketch, "E40.14.0.0", {"start": v(-72.03, -1.5) * mm, "end": v(-72.03, -5.5) * mm});
            skLineSegment(sketch, "E40.14.0.1", {"start": v(-68.03, -1.5) * mm, "end": v(-68.03, -5.5) * mm});
            skLineSegment(sketch, "E40.14.0.2", {"start": v(-73.03, -5.5) * mm, "end": v(-72.03, -5.5) * mm, "construction": true});
            skLineSegment(sketch, "E40.14.0.3", {"start": v(-71.98, -1.5) * mm, "end": v(-71.98, -5.5) * mm});
            skLineSegment(sketch, "E40.14.0.4", {"start": v(-67.98, -1.5) * mm, "end": v(-67.98, -5.5) * mm});
            skLineSegment(sketch, "E40.14.0.5", {"start": v(-72.98, -1.5) * mm, "end": v(-72.98, -5.5) * mm});
            skLineSegment(sketch, "E40.14.0.6", {"start": v(-67.03, -1.5) * mm, "end": v(-67.03, -5.5) * mm});
            skLineSegment(sketch, "E40.14.0.7", {"start": v(-71.03, -1.5) * mm, "end": v(-71.03, -5.5) * mm});
            skLineSegment(sketch, "E40.14.0.8", {"start": v(-69.98, -1.5) * mm, "end": v(-69.98, -5.5) * mm});
            skLineSegment(sketch, "E40.14.0.9", {"start": v(-65.98, -1.5) * mm, "end": v(-65.98, -5.5) * mm});
            skLineSegment(sketch, "E40.14.0.10", {"start": v(-70.03, -1.5) * mm, "end": v(-70.03, -5.5) * mm});
            skLineSegment(sketch, "E40.14.0.11", {"start": v(-66.03, -1.5) * mm, "end": v(-66.03, -5.5) * mm});
            skLineSegment(sketch, "E40.14.0.12", {"start": v(-65.03, -1.5) * mm, "end": v(-65.03, -5.5) * mm});
            skLineSegment(sketch, "E40.14.0.13", {"start": v(-69.03, -1.5) * mm, "end": v(-69.03, -5.5) * mm});
            skLineSegment(sketch, "E40.14.0.14", {"start": v(-66.98, -1.5) * mm, "end": v(-66.98, -5.5) * mm});
            skLineSegment(sketch, "E40.14.0.15", {"start": v(-70.98, -1.5) * mm, "end": v(-70.98, -5.5) * mm});
            skLineSegment(sketch, "E40.14.0.16", {"start": v(-68.98, -1.5) * mm, "end": v(-68.98, -5.5) * mm});
            skLineSegment(sketch, "E40.14.0.17", {"start": v(-64.98, -1.5) * mm, "end": v(-64.98, -5.5) * mm});
            skLineSegment(sketch, "E40.14.0.18", {"start": v(-73.03, -1.5) * mm, "end": v(-73.03, -5.5) * mm});
            skLineSegment(sketch, "E40.14.0.19", {"start": v(-68.03, -5.5) * mm, "end": v(-67.98, -5.5) * mm});
            skLineSegment(sketch, "E40.14.0.20", {"start": v(-72.03, -1.5) * mm, "end": v(-71.98, -1.5) * mm});
            skLineSegment(sketch, "E40.14.0.21", {"start": v(-68.03, -1.5) * mm, "end": v(-67.98, -1.5) * mm});
            skLineSegment(sketch, "E40.14.0.22", {"start": v(-70.03, -1.5) * mm, "end": v(-69.98, -1.5) * mm});
            skLineSegment(sketch, "E40.14.0.23", {"start": v(-66.03, -1.5) * mm, "end": v(-65.98, -1.5) * mm});
            skLineSegment(sketch, "E40.14.0.24", {"start": v(-70.03, -5.5) * mm, "end": v(-69.98, -5.5) * mm});
            skLineSegment(sketch, "E40.14.0.25", {"start": v(-66.03, -5.5) * mm, "end": v(-65.98, -5.5) * mm});
            skLineSegment(sketch, "E40.14.0.26", {"start": v(-72.03, -5.5) * mm, "end": v(-71.98, -5.5) * mm});
            skLineSegment(sketch, "E40.14.0.27", {"start": v(-65.03, -5.5) * mm, "end": v(-64.98, -5.5) * mm});
            skLineSegment(sketch, "E40.14.0.28", {"start": v(-69.03, -5.5) * mm, "end": v(-68.98, -5.5) * mm});
            skLineSegment(sketch, "E40.14.0.29", {"start": v(-67.03, -1.5) * mm, "end": v(-66.98, -1.5) * mm});
            skLineSegment(sketch, "E40.14.0.30", {"start": v(-71.03, -1.5) * mm, "end": v(-70.98, -1.5) * mm});
            skLineSegment(sketch, "E40.14.0.31", {"start": v(-67.03, -5.5) * mm, "end": v(-66.98, -5.5) * mm});
            skLineSegment(sketch, "E40.14.0.32", {"start": v(-71.03, -5.5) * mm, "end": v(-70.98, -5.5) * mm});
            skLineSegment(sketch, "E40.14.0.33", {"start": v(-73.03, -1.5) * mm, "end": v(-72.98, -1.5) * mm});
            skLineSegment(sketch, "E40.14.0.34", {"start": v(-69.03, -1.5) * mm, "end": v(-68.98, -1.5) * mm});
            skLineSegment(sketch, "E40.14.0.35", {"start": v(-65.03, -1.5) * mm, "end": v(-64.98, -1.5) * mm});
            skLineSegment(sketch, "E40.14.0.36", {"start": v(-73.03, -5.5) * mm, "end": v(-72.98, -5.5) * mm});
            skLineSegment(sketch, "E40.15.0.0", {"start": v(-62.03, -1.5) * mm, "end": v(-62.03, -5.5) * mm});
            skLineSegment(sketch, "E40.15.0.1", {"start": v(-58.03, -1.5) * mm, "end": v(-58.03, -5.5) * mm});
            skLineSegment(sketch, "E40.15.0.2", {"start": v(-63.03, -5.5) * mm, "end": v(-62.03, -5.5) * mm, "construction": true});
            skLineSegment(sketch, "E40.15.0.3", {"start": v(-61.98, -1.5) * mm, "end": v(-61.98, -5.5) * mm});
            skLineSegment(sketch, "E40.15.0.4", {"start": v(-57.98, -1.5) * mm, "end": v(-57.98, -5.5) * mm});
            skLineSegment(sketch, "E40.15.0.5", {"start": v(-62.98, -1.5) * mm, "end": v(-62.98, -5.5) * mm});
            skLineSegment(sketch, "E40.15.0.6", {"start": v(-57.03, -1.5) * mm, "end": v(-57.03, -5.5) * mm});
            skLineSegment(sketch, "E40.15.0.7", {"start": v(-61.03, -1.5) * mm, "end": v(-61.03, -5.5) * mm});
            skLineSegment(sketch, "E40.15.0.8", {"start": v(-59.98, -1.5) * mm, "end": v(-59.98, -5.5) * mm});
            skLineSegment(sketch, "E40.15.0.9", {"start": v(-55.98, -1.5) * mm, "end": v(-55.98, -5.5) * mm});
            skLineSegment(sketch, "E40.15.0.10", {"start": v(-60.03, -1.5) * mm, "end": v(-60.03, -5.5) * mm});
            skLineSegment(sketch, "E40.15.0.11", {"start": v(-56.03, -1.5) * mm, "end": v(-56.03, -5.5) * mm});
            skLineSegment(sketch, "E40.15.0.12", {"start": v(-55.03, -1.5) * mm, "end": v(-55.03, -5.5) * mm});
            skLineSegment(sketch, "E40.15.0.13", {"start": v(-59.03, -1.5) * mm, "end": v(-59.03, -5.5) * mm});
            skLineSegment(sketch, "E40.15.0.14", {"start": v(-56.98, -1.5) * mm, "end": v(-56.98, -5.5) * mm});
            skLineSegment(sketch, "E40.15.0.15", {"start": v(-60.98, -1.5) * mm, "end": v(-60.98, -5.5) * mm});
            skLineSegment(sketch, "E40.15.0.16", {"start": v(-58.98, -1.5) * mm, "end": v(-58.98, -5.5) * mm});
            skLineSegment(sketch, "E40.15.0.17", {"start": v(-54.98, -1.5) * mm, "end": v(-54.98, -5.5) * mm});
            skLineSegment(sketch, "E40.15.0.18", {"start": v(-63.03, -1.5) * mm, "end": v(-63.03, -5.5) * mm});
            skLineSegment(sketch, "E40.15.0.19", {"start": v(-58.03, -5.5) * mm, "end": v(-57.98, -5.5) * mm});
            skLineSegment(sketch, "E40.15.0.20", {"start": v(-62.03, -1.5) * mm, "end": v(-61.98, -1.5) * mm});
            skLineSegment(sketch, "E40.15.0.21", {"start": v(-58.03, -1.5) * mm, "end": v(-57.98, -1.5) * mm});
            skLineSegment(sketch, "E40.15.0.22", {"start": v(-60.03, -1.5) * mm, "end": v(-59.98, -1.5) * mm});
            skLineSegment(sketch, "E40.15.0.23", {"start": v(-56.03, -1.5) * mm, "end": v(-55.98, -1.5) * mm});
            skLineSegment(sketch, "E40.15.0.24", {"start": v(-60.03, -5.5) * mm, "end": v(-59.98, -5.5) * mm});
            skLineSegment(sketch, "E40.15.0.25", {"start": v(-56.03, -5.5) * mm, "end": v(-55.98, -5.5) * mm});
            skLineSegment(sketch, "E40.15.0.26", {"start": v(-62.03, -5.5) * mm, "end": v(-61.98, -5.5) * mm});
            skLineSegment(sketch, "E40.15.0.27", {"start": v(-55.03, -5.5) * mm, "end": v(-54.98, -5.5) * mm});
            skLineSegment(sketch, "E40.15.0.28", {"start": v(-59.03, -5.5) * mm, "end": v(-58.98, -5.5) * mm});
            skLineSegment(sketch, "E40.15.0.29", {"start": v(-57.03, -1.5) * mm, "end": v(-56.98, -1.5) * mm});
            skLineSegment(sketch, "E40.15.0.30", {"start": v(-61.03, -1.5) * mm, "end": v(-60.98, -1.5) * mm});
            skLineSegment(sketch, "E40.15.0.31", {"start": v(-57.03, -5.5) * mm, "end": v(-56.98, -5.5) * mm});
            skLineSegment(sketch, "E40.15.0.32", {"start": v(-61.03, -5.5) * mm, "end": v(-60.98, -5.5) * mm});
            skLineSegment(sketch, "E40.15.0.33", {"start": v(-63.03, -1.5) * mm, "end": v(-62.98, -1.5) * mm});
            skLineSegment(sketch, "E40.15.0.34", {"start": v(-59.03, -1.5) * mm, "end": v(-58.98, -1.5) * mm});
            skLineSegment(sketch, "E40.15.0.35", {"start": v(-55.03, -1.5) * mm, "end": v(-54.98, -1.5) * mm});
            skLineSegment(sketch, "E40.15.0.36", {"start": v(-63.03, -5.5) * mm, "end": v(-62.98, -5.5) * mm});
            skLineSegment(sketch, "E40.16.0.0", {"start": v(-52.03, -1.5) * mm, "end": v(-52.03, -5.5) * mm});
            skLineSegment(sketch, "E40.16.0.1", {"start": v(-48.03, -1.5) * mm, "end": v(-48.03, -5.5) * mm});
            skLineSegment(sketch, "E40.16.0.2", {"start": v(-53.03, -5.5) * mm, "end": v(-52.03, -5.5) * mm, "construction": true});
            skLineSegment(sketch, "E40.16.0.3", {"start": v(-51.98, -1.5) * mm, "end": v(-51.98, -5.5) * mm});
            skLineSegment(sketch, "E40.16.0.4", {"start": v(-47.98, -1.5) * mm, "end": v(-47.98, -5.5) * mm});
            skLineSegment(sketch, "E40.16.0.5", {"start": v(-52.98, -1.5) * mm, "end": v(-52.98, -5.5) * mm});
            skLineSegment(sketch, "E40.16.0.6", {"start": v(-47.03, -1.5) * mm, "end": v(-47.03, -5.5) * mm});
            skLineSegment(sketch, "E40.16.0.7", {"start": v(-51.03, -1.5) * mm, "end": v(-51.03, -5.5) * mm});
            skLineSegment(sketch, "E40.16.0.8", {"start": v(-49.98, -1.5) * mm, "end": v(-49.98, -5.5) * mm});
            skLineSegment(sketch, "E40.16.0.9", {"start": v(-45.98, -1.5) * mm, "end": v(-45.98, -5.5) * mm});
            skLineSegment(sketch, "E40.16.0.10", {"start": v(-50.03, -1.5) * mm, "end": v(-50.03, -5.5) * mm});
            skLineSegment(sketch, "E40.16.0.11", {"start": v(-46.03, -1.5) * mm, "end": v(-46.03, -5.5) * mm});
            skLineSegment(sketch, "E40.16.0.12", {"start": v(-45.03, -1.5) * mm, "end": v(-45.03, -5.5) * mm});
            skLineSegment(sketch, "E40.16.0.13", {"start": v(-49.03, -1.5) * mm, "end": v(-49.03, -5.5) * mm});
            skLineSegment(sketch, "E40.16.0.14", {"start": v(-46.98, -1.5) * mm, "end": v(-46.98, -5.5) * mm});
            skLineSegment(sketch, "E40.16.0.15", {"start": v(-50.98, -1.5) * mm, "end": v(-50.98, -5.5) * mm});
            skLineSegment(sketch, "E40.16.0.16", {"start": v(-48.98, -1.5) * mm, "end": v(-48.98, -5.5) * mm});
            skLineSegment(sketch, "E40.16.0.17", {"start": v(-44.98, -1.5) * mm, "end": v(-44.98, -5.5) * mm});
            skLineSegment(sketch, "E40.16.0.18", {"start": v(-53.03, -1.5) * mm, "end": v(-53.03, -5.5) * mm});
            skLineSegment(sketch, "E40.16.0.19", {"start": v(-48.03, -5.5) * mm, "end": v(-47.98, -5.5) * mm});
            skLineSegment(sketch, "E40.16.0.20", {"start": v(-52.03, -1.5) * mm, "end": v(-51.98, -1.5) * mm});
            skLineSegment(sketch, "E40.16.0.21", {"start": v(-48.03, -1.5) * mm, "end": v(-47.98, -1.5) * mm});
            skLineSegment(sketch, "E40.16.0.22", {"start": v(-50.03, -1.5) * mm, "end": v(-49.98, -1.5) * mm});
            skLineSegment(sketch, "E40.16.0.23", {"start": v(-46.03, -1.5) * mm, "end": v(-45.98, -1.5) * mm});
            skLineSegment(sketch, "E40.16.0.24", {"start": v(-50.03, -5.5) * mm, "end": v(-49.98, -5.5) * mm});
            skLineSegment(sketch, "E40.16.0.25", {"start": v(-46.03, -5.5) * mm, "end": v(-45.98, -5.5) * mm});
            skLineSegment(sketch, "E40.16.0.26", {"start": v(-52.03, -5.5) * mm, "end": v(-51.98, -5.5) * mm});
            skLineSegment(sketch, "E40.16.0.27", {"start": v(-45.03, -5.5) * mm, "end": v(-44.98, -5.5) * mm});
            skLineSegment(sketch, "E40.16.0.28", {"start": v(-49.03, -5.5) * mm, "end": v(-48.98, -5.5) * mm});
            skLineSegment(sketch, "E40.16.0.29", {"start": v(-47.03, -1.5) * mm, "end": v(-46.98, -1.5) * mm});
            skLineSegment(sketch, "E40.16.0.30", {"start": v(-51.03, -1.5) * mm, "end": v(-50.98, -1.5) * mm});
            skLineSegment(sketch, "E40.16.0.31", {"start": v(-47.03, -5.5) * mm, "end": v(-46.98, -5.5) * mm});
            skLineSegment(sketch, "E40.16.0.32", {"start": v(-51.03, -5.5) * mm, "end": v(-50.98, -5.5) * mm});
            skLineSegment(sketch, "E40.16.0.33", {"start": v(-53.03, -1.5) * mm, "end": v(-52.98, -1.5) * mm});
            skLineSegment(sketch, "E40.16.0.34", {"start": v(-49.03, -1.5) * mm, "end": v(-48.98, -1.5) * mm});
            skLineSegment(sketch, "E40.16.0.35", {"start": v(-45.03, -1.5) * mm, "end": v(-44.98, -1.5) * mm});
            skLineSegment(sketch, "E40.16.0.36", {"start": v(-53.03, -5.5) * mm, "end": v(-52.98, -5.5) * mm});
            skLineSegment(sketch, "E40.17.0.0", {"start": v(-42.03, -1.5) * mm, "end": v(-42.03, -5.5) * mm});
            skLineSegment(sketch, "E40.17.0.1", {"start": v(-38.03, -1.5) * mm, "end": v(-38.03, -5.5) * mm});
            skLineSegment(sketch, "E40.17.0.2", {"start": v(-43.03, -5.5) * mm, "end": v(-42.03, -5.5) * mm, "construction": true});
            skLineSegment(sketch, "E40.17.0.3", {"start": v(-41.98, -1.5) * mm, "end": v(-41.98, -5.5) * mm});
            skLineSegment(sketch, "E40.17.0.4", {"start": v(-37.98, -1.5) * mm, "end": v(-37.98, -5.5) * mm});
            skLineSegment(sketch, "E40.17.0.5", {"start": v(-42.98, -1.5) * mm, "end": v(-42.98, -5.5) * mm});
            skLineSegment(sketch, "E40.17.0.6", {"start": v(-37.03, -1.5) * mm, "end": v(-37.03, -5.5) * mm});
            skLineSegment(sketch, "E40.17.0.7", {"start": v(-41.03, -1.5) * mm, "end": v(-41.03, -5.5) * mm});
            skLineSegment(sketch, "E40.17.0.8", {"start": v(-39.98, -1.5) * mm, "end": v(-39.98, -5.5) * mm});
            skLineSegment(sketch, "E40.17.0.9", {"start": v(-35.98, -1.5) * mm, "end": v(-35.98, -5.5) * mm});
            skLineSegment(sketch, "E40.17.0.10", {"start": v(-40.03, -1.5) * mm, "end": v(-40.03, -5.5) * mm});
            skLineSegment(sketch, "E40.17.0.11", {"start": v(-36.03, -1.5) * mm, "end": v(-36.03, -5.5) * mm});
            skLineSegment(sketch, "E40.17.0.12", {"start": v(-35.03, -1.5) * mm, "end": v(-35.03, -5.5) * mm});
            skLineSegment(sketch, "E40.17.0.13", {"start": v(-39.03, -1.5) * mm, "end": v(-39.03, -5.5) * mm});
            skLineSegment(sketch, "E40.17.0.14", {"start": v(-36.98, -1.5) * mm, "end": v(-36.98, -5.5) * mm});
            skLineSegment(sketch, "E40.17.0.15", {"start": v(-40.98, -1.5) * mm, "end": v(-40.98, -5.5) * mm});
            skLineSegment(sketch, "E40.17.0.16", {"start": v(-38.98, -1.5) * mm, "end": v(-38.98, -5.5) * mm});
            skLineSegment(sketch, "E40.17.0.17", {"start": v(-34.98, -1.5) * mm, "end": v(-34.98, -5.5) * mm});
            skLineSegment(sketch, "E40.17.0.18", {"start": v(-43.03, -1.5) * mm, "end": v(-43.03, -5.5) * mm});
            skLineSegment(sketch, "E40.17.0.19", {"start": v(-38.03, -5.5) * mm, "end": v(-37.98, -5.5) * mm});
            skLineSegment(sketch, "E40.17.0.20", {"start": v(-42.03, -1.5) * mm, "end": v(-41.98, -1.5) * mm});
            skLineSegment(sketch, "E40.17.0.21", {"start": v(-38.03, -1.5) * mm, "end": v(-37.98, -1.5) * mm});
            skLineSegment(sketch, "E40.17.0.22", {"start": v(-40.03, -1.5) * mm, "end": v(-39.98, -1.5) * mm});
            skLineSegment(sketch, "E40.17.0.23", {"start": v(-36.03, -1.5) * mm, "end": v(-35.98, -1.5) * mm});
            skLineSegment(sketch, "E40.17.0.24", {"start": v(-40.03, -5.5) * mm, "end": v(-39.98, -5.5) * mm});
            skLineSegment(sketch, "E40.17.0.25", {"start": v(-36.03, -5.5) * mm, "end": v(-35.98, -5.5) * mm});
            skLineSegment(sketch, "E40.17.0.26", {"start": v(-42.03, -5.5) * mm, "end": v(-41.98, -5.5) * mm});
            skLineSegment(sketch, "E40.17.0.27", {"start": v(-35.03, -5.5) * mm, "end": v(-34.98, -5.5) * mm});
            skLineSegment(sketch, "E40.17.0.28", {"start": v(-39.03, -5.5) * mm, "end": v(-38.98, -5.5) * mm});
            skLineSegment(sketch, "E40.17.0.29", {"start": v(-37.03, -1.5) * mm, "end": v(-36.98, -1.5) * mm});
            skLineSegment(sketch, "E40.17.0.30", {"start": v(-41.03, -1.5) * mm, "end": v(-40.98, -1.5) * mm});
            skLineSegment(sketch, "E40.17.0.31", {"start": v(-37.03, -5.5) * mm, "end": v(-36.98, -5.5) * mm});
            skLineSegment(sketch, "E40.17.0.32", {"start": v(-41.03, -5.5) * mm, "end": v(-40.98, -5.5) * mm});
            skLineSegment(sketch, "E40.17.0.33", {"start": v(-43.03, -1.5) * mm, "end": v(-42.98, -1.5) * mm});
            skLineSegment(sketch, "E40.17.0.34", {"start": v(-39.03, -1.5) * mm, "end": v(-38.98, -1.5) * mm});
            skLineSegment(sketch, "E40.17.0.35", {"start": v(-35.03, -1.5) * mm, "end": v(-34.98, -1.5) * mm});
            skLineSegment(sketch, "E40.17.0.36", {"start": v(-43.03, -5.5) * mm, "end": v(-42.98, -5.5) * mm});
            skLineSegment(sketch, "E40.18.0.0", {"start": v(-32.03, -1.5) * mm, "end": v(-32.03, -5.5) * mm});
            skLineSegment(sketch, "E40.18.0.1", {"start": v(-28.03, -1.5) * mm, "end": v(-28.03, -5.5) * mm});
            skLineSegment(sketch, "E40.18.0.2", {"start": v(-33.03, -5.5) * mm, "end": v(-32.03, -5.5) * mm, "construction": true});
            skLineSegment(sketch, "E40.18.0.3", {"start": v(-31.98, -1.5) * mm, "end": v(-31.98, -5.5) * mm});
            skLineSegment(sketch, "E40.18.0.4", {"start": v(-27.98, -1.5) * mm, "end": v(-27.98, -5.5) * mm});
            skLineSegment(sketch, "E40.18.0.5", {"start": v(-32.98, -1.5) * mm, "end": v(-32.98, -5.5) * mm});
            skLineSegment(sketch, "E40.18.0.6", {"start": v(-27.03, -1.5) * mm, "end": v(-27.03, -5.5) * mm});
            skLineSegment(sketch, "E40.18.0.7", {"start": v(-31.03, -1.5) * mm, "end": v(-31.03, -5.5) * mm});
            skLineSegment(sketch, "E40.18.0.8", {"start": v(-29.98, -1.5) * mm, "end": v(-29.98, -5.5) * mm});
            skLineSegment(sketch, "E40.18.0.9", {"start": v(-25.98, -1.5) * mm, "end": v(-25.98, -5.5) * mm});
            skLineSegment(sketch, "E40.18.0.10", {"start": v(-30.03, -1.5) * mm, "end": v(-30.03, -5.5) * mm});
            skLineSegment(sketch, "E40.18.0.11", {"start": v(-26.03, -1.5) * mm, "end": v(-26.03, -5.5) * mm});
            skLineSegment(sketch, "E40.18.0.12", {"start": v(-25.03, -1.5) * mm, "end": v(-25.03, -5.5) * mm});
            skLineSegment(sketch, "E40.18.0.13", {"start": v(-29.03, -1.5) * mm, "end": v(-29.03, -5.5) * mm});
            skLineSegment(sketch, "E40.18.0.14", {"start": v(-26.98, -1.5) * mm, "end": v(-26.98, -5.5) * mm});
            skLineSegment(sketch, "E40.18.0.15", {"start": v(-30.98, -1.5) * mm, "end": v(-30.98, -5.5) * mm});
            skLineSegment(sketch, "E40.18.0.16", {"start": v(-28.98, -1.5) * mm, "end": v(-28.98, -5.5) * mm});
            skLineSegment(sketch, "E40.18.0.17", {"start": v(-24.98, -1.5) * mm, "end": v(-24.98, -5.5) * mm});
            skLineSegment(sketch, "E40.18.0.18", {"start": v(-33.03, -1.5) * mm, "end": v(-33.03, -5.5) * mm});
            skLineSegment(sketch, "E40.18.0.19", {"start": v(-28.03, -5.5) * mm, "end": v(-27.98, -5.5) * mm});
            skLineSegment(sketch, "E40.18.0.20", {"start": v(-32.03, -1.5) * mm, "end": v(-31.98, -1.5) * mm});
            skLineSegment(sketch, "E40.18.0.21", {"start": v(-28.03, -1.5) * mm, "end": v(-27.98, -1.5) * mm});
            skLineSegment(sketch, "E40.18.0.22", {"start": v(-30.03, -1.5) * mm, "end": v(-29.98, -1.5) * mm});
            skLineSegment(sketch, "E40.18.0.23", {"start": v(-26.03, -1.5) * mm, "end": v(-25.98, -1.5) * mm});
            skLineSegment(sketch, "E40.18.0.24", {"start": v(-30.03, -5.5) * mm, "end": v(-29.98, -5.5) * mm});
            skLineSegment(sketch, "E40.18.0.25", {"start": v(-26.03, -5.5) * mm, "end": v(-25.98, -5.5) * mm});
            skLineSegment(sketch, "E40.18.0.26", {"start": v(-32.03, -5.5) * mm, "end": v(-31.98, -5.5) * mm});
            skLineSegment(sketch, "E40.18.0.27", {"start": v(-25.03, -5.5) * mm, "end": v(-24.98, -5.5) * mm});
            skLineSegment(sketch, "E40.18.0.28", {"start": v(-29.03, -5.5) * mm, "end": v(-28.98, -5.5) * mm});
            skLineSegment(sketch, "E40.18.0.29", {"start": v(-27.03, -1.5) * mm, "end": v(-26.98, -1.5) * mm});
            skLineSegment(sketch, "E40.18.0.30", {"start": v(-31.03, -1.5) * mm, "end": v(-30.98, -1.5) * mm});
            skLineSegment(sketch, "E40.18.0.31", {"start": v(-27.03, -5.5) * mm, "end": v(-26.98, -5.5) * mm});
            skLineSegment(sketch, "E40.18.0.32", {"start": v(-31.03, -5.5) * mm, "end": v(-30.98, -5.5) * mm});
            skLineSegment(sketch, "E40.18.0.33", {"start": v(-33.03, -1.5) * mm, "end": v(-32.98, -1.5) * mm});
            skLineSegment(sketch, "E40.18.0.34", {"start": v(-29.03, -1.5) * mm, "end": v(-28.98, -1.5) * mm});
            skLineSegment(sketch, "E40.18.0.35", {"start": v(-25.03, -1.5) * mm, "end": v(-24.98, -1.5) * mm});
            skLineSegment(sketch, "E40.18.0.36", {"start": v(-33.03, -5.5) * mm, "end": v(-32.98, -5.5) * mm});
            skLineSegment(sketch, "E40.19.0.0", {"start": v(-22.03, -1.5) * mm, "end": v(-22.03, -5.5) * mm});
            skLineSegment(sketch, "E40.19.0.1", {"start": v(-18.03, -1.5) * mm, "end": v(-18.03, -5.5) * mm});
            skLineSegment(sketch, "E40.19.0.2", {"start": v(-23.03, -5.5) * mm, "end": v(-22.03, -5.5) * mm, "construction": true});
            skLineSegment(sketch, "E40.19.0.3", {"start": v(-21.98, -1.5) * mm, "end": v(-21.98, -5.5) * mm});
            skLineSegment(sketch, "E40.19.0.4", {"start": v(-17.98, -1.5) * mm, "end": v(-17.98, -5.5) * mm});
            skLineSegment(sketch, "E40.19.0.5", {"start": v(-22.98, -1.5) * mm, "end": v(-22.98, -5.5) * mm});
            skLineSegment(sketch, "E40.19.0.6", {"start": v(-17.03, -1.5) * mm, "end": v(-17.03, -5.5) * mm});
            skLineSegment(sketch, "E40.19.0.7", {"start": v(-21.03, -1.5) * mm, "end": v(-21.03, -5.5) * mm});
            skLineSegment(sketch, "E40.19.0.8", {"start": v(-19.98, -1.5) * mm, "end": v(-19.98, -5.5) * mm});
            skLineSegment(sketch, "E40.19.0.9", {"start": v(-15.98, -1.5) * mm, "end": v(-15.98, -5.5) * mm});
            skLineSegment(sketch, "E40.19.0.10", {"start": v(-20.03, -1.5) * mm, "end": v(-20.03, -5.5) * mm});
            skLineSegment(sketch, "E40.19.0.11", {"start": v(-16.03, -1.5) * mm, "end": v(-16.03, -5.5) * mm});
            skLineSegment(sketch, "E40.19.0.12", {"start": v(-15.03, -1.5) * mm, "end": v(-15.03, -5.5) * mm});
            skLineSegment(sketch, "E40.19.0.13", {"start": v(-19.03, -1.5) * mm, "end": v(-19.03, -5.5) * mm});
            skLineSegment(sketch, "E40.19.0.14", {"start": v(-16.98, -1.5) * mm, "end": v(-16.98, -5.5) * mm});
            skLineSegment(sketch, "E40.19.0.15", {"start": v(-20.98, -1.5) * mm, "end": v(-20.98, -5.5) * mm});
            skLineSegment(sketch, "E40.19.0.16", {"start": v(-18.98, -1.5) * mm, "end": v(-18.98, -5.5) * mm});
            skLineSegment(sketch, "E40.19.0.17", {"start": v(-14.98, -1.5) * mm, "end": v(-14.98, -5.5) * mm});
            skLineSegment(sketch, "E40.19.0.18", {"start": v(-23.03, -1.5) * mm, "end": v(-23.03, -5.5) * mm});
            skLineSegment(sketch, "E40.19.0.19", {"start": v(-18.03, -5.5) * mm, "end": v(-17.98, -5.5) * mm});
            skLineSegment(sketch, "E40.19.0.20", {"start": v(-22.03, -1.5) * mm, "end": v(-21.98, -1.5) * mm});
            skLineSegment(sketch, "E40.19.0.21", {"start": v(-18.03, -1.5) * mm, "end": v(-17.98, -1.5) * mm});
            skLineSegment(sketch, "E40.19.0.22", {"start": v(-20.03, -1.5) * mm, "end": v(-19.98, -1.5) * mm});
            skLineSegment(sketch, "E40.19.0.23", {"start": v(-16.03, -1.5) * mm, "end": v(-15.98, -1.5) * mm});
            skLineSegment(sketch, "E40.19.0.24", {"start": v(-20.03, -5.5) * mm, "end": v(-19.98, -5.5) * mm});
            skLineSegment(sketch, "E40.19.0.25", {"start": v(-16.03, -5.5) * mm, "end": v(-15.98, -5.5) * mm});
            skLineSegment(sketch, "E40.19.0.26", {"start": v(-22.03, -5.5) * mm, "end": v(-21.98, -5.5) * mm});
            skLineSegment(sketch, "E40.19.0.27", {"start": v(-15.03, -5.5) * mm, "end": v(-14.98, -5.5) * mm});
            skLineSegment(sketch, "E40.19.0.28", {"start": v(-19.03, -5.5) * mm, "end": v(-18.98, -5.5) * mm});
            skLineSegment(sketch, "E40.19.0.29", {"start": v(-17.03, -1.5) * mm, "end": v(-16.98, -1.5) * mm});
            skLineSegment(sketch, "E40.19.0.30", {"start": v(-21.03, -1.5) * mm, "end": v(-20.98, -1.5) * mm});
            skLineSegment(sketch, "E40.19.0.31", {"start": v(-17.03, -5.5) * mm, "end": v(-16.98, -5.5) * mm});
            skLineSegment(sketch, "E40.19.0.32", {"start": v(-21.03, -5.5) * mm, "end": v(-20.98, -5.5) * mm});
            skLineSegment(sketch, "E40.19.0.33", {"start": v(-23.03, -1.5) * mm, "end": v(-22.98, -1.5) * mm});
            skLineSegment(sketch, "E40.19.0.34", {"start": v(-19.03, -1.5) * mm, "end": v(-18.98, -1.5) * mm});
            skLineSegment(sketch, "E40.19.0.35", {"start": v(-15.03, -1.5) * mm, "end": v(-14.98, -1.5) * mm});
            skLineSegment(sketch, "E40.19.0.36", {"start": v(-23.03, -5.5) * mm, "end": v(-22.98, -5.5) * mm});
            skLineSegment(sketch, "E40.direction1", {"start": v(-213.03, -5.5) * mm, "end": v(-203.03, -5.5) * mm, "construction": true});
            skSolve(sketch);
        }
        {
            var Q0;
            Q0=qSketchRegion(id+"F14",true);
            extrude(context, id + "F15", {"entities" : qUnion([Q0]), "operationType" : NewBodyOperationType.REMOVE, "oppositeDirection" : true, "depth" : 0.1 * mm});
        }
        {
            var Q0;
            Q0=makeQuery(id+"F1.opExtrude","CAP_FACE",FACE,{"disambiguationData":[OSD([sQuery(id+"F0.wireOp",EDGE,"E1"),sQuery(id+"F0.wireOp",EDGE,"E2"),sQuery(id+"F0.wireOp",EDGE,"E3"),sQuery(id+"F0.wireOp",EDGE,"E4"),sQuery(id+"F0.wireOp",EDGE,"E5.MirrorCS"),sQuery(id+"F0.wireOp",EDGE,"E6.MirrorCS"),sQuery(id+"F0.wireOp",EDGE,"E7.MirrorCS"),sQuery(id+"F0.wireOp",EDGE,"E8"),sQuery(id+"F0.wireOp",EDGE,"E9"),sQuery(id+"F0.wireOp",EDGE,"E10"),sQuery(id+"F0.wireOp",EDGE,"E11"),sQuery(id+"F0.wireOp",EDGE,"E12"),sQuery(id+"F0.wireOp",EDGE,"E14"),sQuery(id+"F0.wireOp",EDGE,"E15"),sQuery(id+"F0.wireOp",EDGE,"E16"),sQuery(id+"F0.wireOp",EDGE,"E17"),sQuery(id+"F0.wireOp",EDGE,"E18"),sQuery(id+"F0.wireOp",EDGE,"E19"),sQuery(id+"F0.wireOp",EDGE,"E20"),sQuery(id+"F0.wireOp",EDGE,"E21.filletArc"),sQuery(id+"F0.wireOp",EDGE,"E22.filletArc")])],"isStart":false});
            var sketch = newSketch(context, id + "F16", { "sketchPlane" : qUnion([Q0])});
            skLineSegment(sketch, "E41", {"start": v(-213.98, 1.5) * mm, "end": v(-9.64, 1.5) * mm, "construction": true});
            skText(sketch, "E42", { "text": "1", "fontName": "OpenSans-Regular.ttf"});
            skText(sketch, "E43", { "text": "2", "fontName": "OpenSans-Regular.ttf"});
            skText(sketch, "E44", { "text": "3", "fontName": "OpenSans-Regular.ttf"});
            skText(sketch, "E45", { "text": "4", "fontName": "OpenSans-Regular.ttf"});
            skText(sketch, "E46", { "text": "5", "fontName": "OpenSans-Regular.ttf"});
            skText(sketch, "E47", { "text": "6", "fontName": "OpenSans-Regular.ttf"});
            skLineSegment(sketch, "E48", {"start": v(-212.83, 3.5) * mm, "end": v(-11.77, 3.5) * mm, "construction": true});
            skText(sketch, "E49", { "text": "7", "fontName": "OpenSans-Regular.ttf"});
            skText(sketch, "E50", { "text": "8", "fontName": "OpenSans-Regular.ttf"});
            skText(sketch, "E51", { "text": "9", "fontName": "OpenSans-Regular.ttf"});
            skText(sketch, "E52", { "text": "10", "fontName": "OpenSans-Regular.ttf"});
            skText(sketch, "E53", { "text": "11", "fontName": "OpenSans-Regular.ttf"});
            skText(sketch, "E54", { "text": "12", "fontName": "OpenSans-Regular.ttf"});
            skText(sketch, "E55", { "text": "13", "fontName": "OpenSans-Regular.ttf"});
            skText(sketch, "E56", { "text": "14", "fontName": "OpenSans-Regular.ttf"});
            skText(sketch, "E57", { "text": "15", "fontName": "OpenSans-Regular.ttf"});
            skText(sketch, "E58", { "text": "16", "fontName": "OpenSans-Regular.ttf"});
            skText(sketch, "E59", { "text": "17", "fontName": "OpenSans-Regular.ttf"});
            skText(sketch, "E60", { "text": "18", "fontName": "OpenSans-Regular.ttf"});
            skText(sketch, "E61", { "text": "19", "fontName": "OpenSans-Regular.ttf"});
            skText(sketch, "E62", { "text": "20", "fontName": "OpenSans-Regular.ttf"});
            const initialGuessF16  = {"E42": [-0.21398, 0.0015, 1, 0, 0.002], "E43": [-0.20398, 0.0015, 1, 0, 0.002], "E44": [-0.19398, 0.0015, 1, 0, 0.002], "E45": [-0.18398, 0.0015, 1, 0, 0.002], "E46": [-0.17398, 0.0015, 1, 0, 0.002], "E47": [-0.16398, 0.0015, 1, 0, 0.002], "E49": [-0.15398, 0.0015, 1, 0, 0.002], "E50": [-0.14398, 0.0015, 1, 0, 0.002], "E51": [-0.13398, 0.0015, 1, 0, 0.002], "E52": [-0.12398, 0.0015, 1, 0, 0.002], "E53": [-0.11398, 0.0015, 1, 0, 0.002], "E54": [-0.10398, 0.0015, 1, 0, 0.002], "E55": [-0.09398, 0.0015, 1, 0, 0.002], "E56": [-0.08398, 0.0015, 1, 0, 0.002], "E57": [-0.07398, 0.0015, 1, 0, 0.002], "E58": [-0.06398, 0.0015, 1, 0, 0.002], "E59": [-0.05398, 0.0015, 1, 0, 0.002], "E60": [-0.04398, 0.0015, 1, 0, 0.002], "E61": [-0.03398, 0.0015, 1, 0, 0.002], "E62": [-0.02398, 0.0015, 1, 0, 0.002]};
            skSetInitialGuess(sketch, initialGuessF16);
            skSolve(sketch);
        }
        {
            var Q0;
            Q0=qSketchRegion(id+"F16",true);
            extrude(context, id + "F17", {"entities" : qUnion([Q0]), "operationType" : NewBodyOperationType.REMOVE, "oppositeDirection" : true, "depth" : 0.1 * mm});
        }
    });
